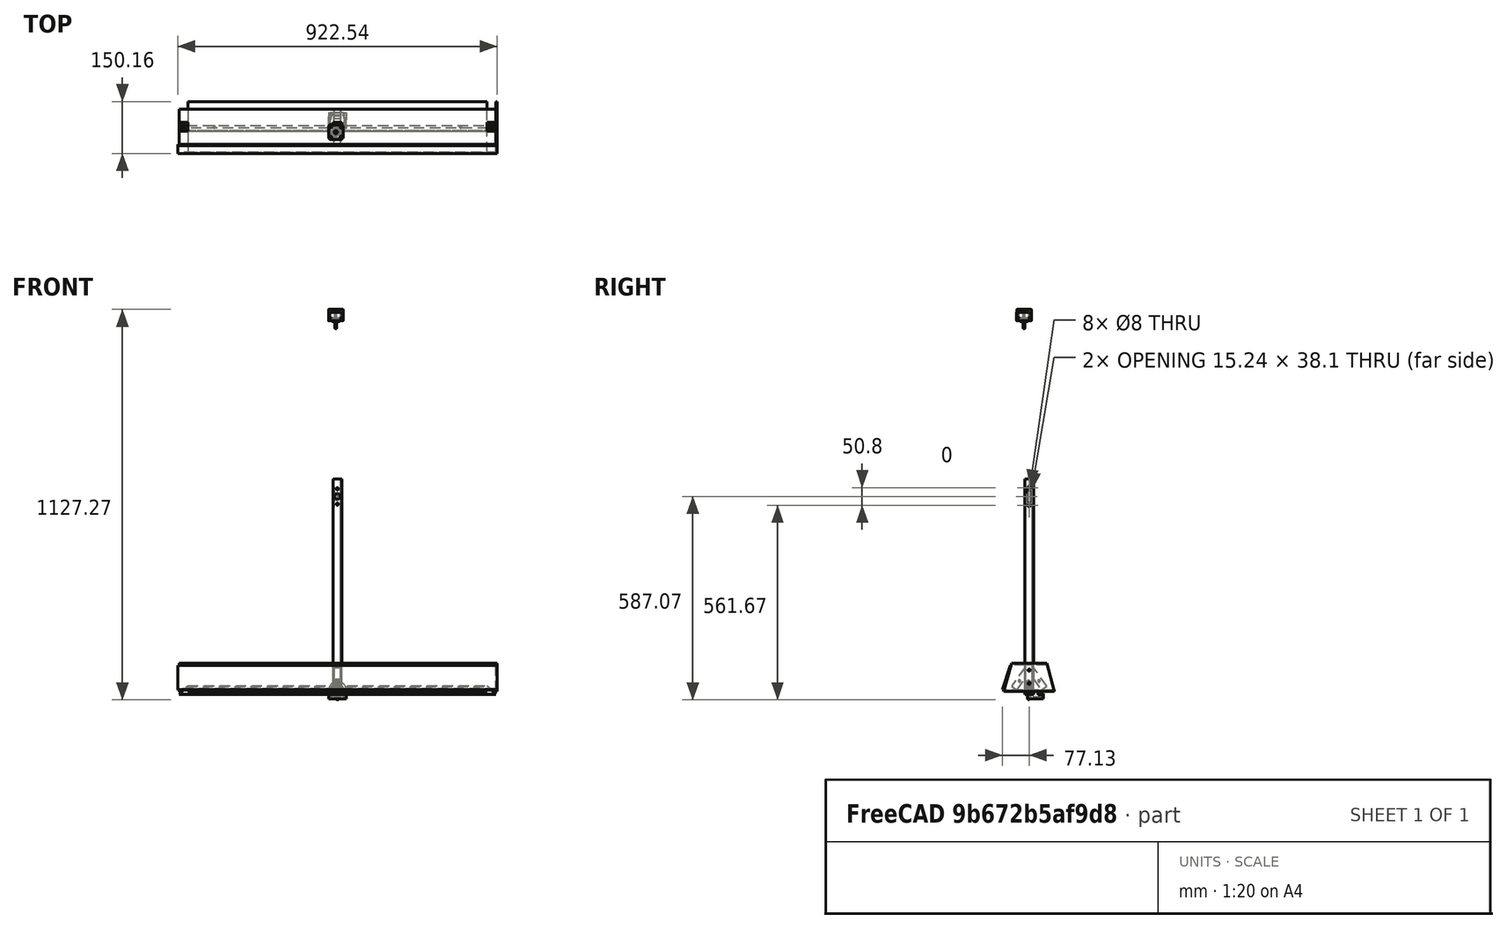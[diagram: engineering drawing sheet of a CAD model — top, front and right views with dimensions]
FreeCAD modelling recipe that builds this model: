
FCSTD DOCUMENT  (FreeCAD 0.21R32637 (Git))
Label: Frame
License: All rights reserved
LicenseURL: http://en.wikipedia.org/wiki/All_rights_reserved
objects: Sketcher::SketchObject×37, PartDesign::Pocket×19, PartDesign::Pad×17, PartDesign::CoordinateSystem×17, TechDraw::DrawViewDimension×16, PartDesign::Body×15, App::Link×8, App::DocumentObjectGroup×3, PartDesign::Plane×3, TechDraw::DrawViewPart×3, TechDraw::DrawSVGTemplate×2, TechDraw::DrawProjGroupItem×2, TechDraw::DrawPage×2, PartDesign::Fillet×2, App::FeaturePython×1, Part::Feature×1, PartDesign::FeatureBase×1, App::Part×1, TechDraw::DrawProjGroup×1, TechDraw::DrawViewDetail×1, +3 more types
note: 173 computed .brp shape members not serialized (recipe doc carries the construction recipe); baked Part::Feature solids carry a one-line shape summary decoded from their .brp

FEATURE [Sketcher::SketchObject] Sketch
  FullyConstrained = true
  MapMode = 5
  Support = -> [XY_Plane]
  sketch-geometry (15):
    g0: LineSegment StartX=-12.7 StartY=-12.7 StartZ=0 EndX=-12.7 EndY=12.7 EndZ=0
    g1: LineSegment StartX=-12.7 StartY=12.7 StartZ=0 EndX=12.7 EndY=12.7 EndZ=0
    g2: LineSegment StartX=12.7 StartY=12.7 StartZ=0 EndX=12.7 EndY=-12.7 EndZ=0
    g3: LineSegment StartX=12.7 StartY=-12.7 StartZ=0 EndX=-12.7 EndY=-12.7 EndZ=0
    g4: GeomPoint X=0 Y=0 Z=0
    g5: ArcOfCircle CenterX=-6.35 CenterY=-6.35 CenterZ=0 NormalX=0 NormalY=0 NormalZ=1 AngleXU=0 Radius=3.175 StartAngle=3.14159 EndAngle=4.71239
    g6: LineSegment StartX=-9.525 StartY=-6.35 StartZ=0 EndX=-9.525 EndY=6.35 EndZ=0
    g7: ArcOfCircle CenterX=-6.35 CenterY=6.35 CenterZ=0 NormalX=0 NormalY=0 NormalZ=1 AngleXU=0 Radius=3.175 StartAngle=1.5708 EndAngle=3.14159
    g8: LineSegment StartX=-6.35 StartY=9.525 StartZ=0 EndX=6.35 EndY=9.525 EndZ=0
    g9: ArcOfCircle CenterX=6.35 CenterY=6.35 CenterZ=0 NormalX=0 NormalY=0 NormalZ=1 AngleXU=0 Radius=3.175 StartAngle=3e-16 EndAngle=1.5708
    g10: LineSegment StartX=9.525 StartY=6.35 StartZ=0 EndX=9.525 EndY=-6.35 EndZ=0
    g11: ArcOfCircle CenterX=6.35 CenterY=-6.35 CenterZ=0 NormalX=0 NormalY=0 NormalZ=1 AngleXU=0 Radius=3.175 StartAngle=4.71239 EndAngle=6.28319
    g12: LineSegment StartX=6.35 StartY=-9.525 StartZ=0 EndX=-6.35 EndY=-9.525 EndZ=0
    g13: GeomPoint X=-9.525 Y=-9.525 Z=0
    g14: GeomPoint X=9.525 Y=9.525 Z=0
  constraints (35):
    c: Coincident(g0,g1)
    c: Coincident(g1,g2)
    c: Coincident(g2,g3)
    c: Coincident(g3,g0)
    c: Horizontal(g1)
    c: Horizontal(g3)
    c: Vertical(g0)
    c: Vertical(g2)
    c: Symmetric(g1,g0,g4)
    c: Coincident(g4,g-1)
    c: Equal(g1,g2)
    c: Distance(g1) = 25.4
    c: Tangent(g5,g6) = 1.5708
    c: Tangent(g6,g7) = 1.5708
    c: Tangent(g7,g8) = 1.5708
    c: Tangent(g8,g9) = 1.5708
    c: Tangent(g9,g10) = 1.5708
    c: Tangent(g10,g11) = 1.5708
    c: Tangent(g11,g12) = 1.5708
    c: Tangent(g12,g5) = 1.5708
    c: Horizontal(g8)
    c: Horizontal(g12)
    c: Vertical(g6)
    c: Vertical(g10)
    c: Equal(g5,g7)
    c: Equal(g7,g9)
    c: Equal(g9,g11)
    c: PointOnObject(g13,g6)
    c: PointOnObject(g13,g12)
    c: PointOnObject(g14,g8)
    c: PointOnObject(g14,g10)
    c: Radius(g9) = 3.175
    c: Symmetric(g7,g11,g4)
    c: Distance(g7,g1) = 3.175
    c: Equal(g8,g6)
FEATURE [PartDesign::Pad] Pad
  Direction = (0,0,1)
  Length = 609.6
  Length2 = 10
  Profile = -> Sketch
  ReferenceAxis = -> Sketch [N_Axis]
  Type = 0
FEATURE [PartDesign::Body] Body  label="Base Extrusion"
  Group = -> [Sketch,Pad]
  Origin = -> Origin
  Tip = -> Pad
FEATURE [Sketcher::SketchObject] Sketch001
  FullyConstrained = true
  MapMode = 5
  Support = -> [XY_Plane001]
  sketch-geometry (15):
    g0: LineSegment StartX=-12.7 StartY=-12.7 StartZ=0 EndX=-12.7 EndY=12.7 EndZ=0
    g1: LineSegment StartX=-12.7 StartY=12.7 StartZ=0 EndX=12.7 EndY=12.7 EndZ=0
    g2: LineSegment StartX=12.7 StartY=12.7 StartZ=0 EndX=12.7 EndY=-12.7 EndZ=0
    g3: LineSegment StartX=12.7 StartY=-12.7 StartZ=0 EndX=-12.7 EndY=-12.7 EndZ=0
    g4: GeomPoint X=0 Y=0 Z=0
    g5: ArcOfCircle CenterX=-6.35 CenterY=-6.35 CenterZ=0 NormalX=0 NormalY=0 NormalZ=1 AngleXU=0 Radius=3.175 StartAngle=3.14159 EndAngle=4.71239
    g6: LineSegment StartX=-9.525 StartY=-6.35 StartZ=0 EndX=-9.525 EndY=6.35 EndZ=0
    g7: ArcOfCircle CenterX=-6.35 CenterY=6.35 CenterZ=0 NormalX=0 NormalY=0 NormalZ=1 AngleXU=0 Radius=3.175 StartAngle=1.5708 EndAngle=3.14159
    g8: LineSegment StartX=-6.35 StartY=9.525 StartZ=0 EndX=6.35 EndY=9.525 EndZ=0
    g9: ArcOfCircle CenterX=6.35 CenterY=6.35 CenterZ=0 NormalX=0 NormalY=0 NormalZ=1 AngleXU=0 Radius=3.175 StartAngle=3e-16 EndAngle=1.5708
    g10: LineSegment StartX=9.525 StartY=6.35 StartZ=0 EndX=9.525 EndY=-6.35 EndZ=0
    g11: ArcOfCircle CenterX=6.35 CenterY=-6.35 CenterZ=0 NormalX=0 NormalY=0 NormalZ=1 AngleXU=0 Radius=3.175 StartAngle=4.71239 EndAngle=6.28319
    g12: LineSegment StartX=6.35 StartY=-9.525 StartZ=0 EndX=-6.35 EndY=-9.525 EndZ=0
    g13: GeomPoint X=-9.525 Y=-9.525 Z=0
    g14: GeomPoint X=9.525 Y=9.525 Z=0
  constraints (35):
    c: Coincident(g0,g1)
    c: Coincident(g1,g2)
    c: Coincident(g2,g3)
    c: Coincident(g3,g0)
    c: Horizontal(g1)
    c: Horizontal(g3)
    c: Vertical(g0)
    c: Vertical(g2)
    c: Symmetric(g1,g0,g4)
    c: Coincident(g4,g-1)
    c: Equal(g1,g2)
    c: Distance(g1) = 25.4
    c: Tangent(g5,g6) = 1.5708
    c: Tangent(g6,g7) = 1.5708
    c: Tangent(g7,g8) = 1.5708
    c: Tangent(g8,g9) = 1.5708
    c: Tangent(g9,g10) = 1.5708
    c: Tangent(g10,g11) = 1.5708
    c: Tangent(g11,g12) = 1.5708
    c: Tangent(g12,g5) = 1.5708
    c: Horizontal(g8)
    c: Horizontal(g12)
    c: Vertical(g6)
    c: Vertical(g10)
    c: Equal(g5,g7)
    c: Equal(g7,g9)
    c: Equal(g9,g11)
    c: PointOnObject(g13,g6)
    c: PointOnObject(g13,g12)
    c: PointOnObject(g14,g8)
    c: PointOnObject(g14,g10)
    c: Radius(g9) = 3.175
    c: Symmetric(g7,g11,g4)
    c: Distance(g7,g1) = 3.175
    c: Equal(g8,g6)
FEATURE [PartDesign::Pad] Pad001
  Direction = (0,0,1)
  Length = 609.6
  Length2 = 10
  Profile = -> Sketch001
  ReferenceAxis = -> Sketch001 [N_Axis]
  Type = 0
FEATURE [Sketcher::SketchObject] Sketch002
  ExternalGeometry = -> [Pad001]
  FullyConstrained = true
  MapMode = 5
  Placement = pos=(0,12.7,0) rot=(0,0.707107,0.707107;3.14159rad)
  Support = -> [Pad001]
  sketch-geometry (8):
    g0: LineSegment StartX=0 StartY=580.72 StartZ=0 EndX=-21.9203 EndY=558.8 EndZ=0
    g1: LineSegment StartX=-21.9203 StartY=558.8 StartZ=0 EndX=0 EndY=536.88 EndZ=0
    g2: LineSegment StartX=0 StartY=536.88 StartZ=0 EndX=21.9203 EndY=558.8 EndZ=0
    g3: LineSegment StartX=21.9203 StartY=558.8 StartZ=0 EndX=0 EndY=580.72 EndZ=0
    g4: LineSegment StartX=21.9203 StartY=558.8 StartZ=0 EndX=-21.9203 EndY=558.8 EndZ=0
    g5: Circle CenterX=0 CenterY=558.8 CenterZ=0 NormalX=0 NormalY=0 NormalZ=1 AngleXU=0 Radius=8.89
    g6: Circle CenterX=0 CenterY=580.72 CenterZ=0 NormalX=0 NormalY=0 NormalZ=1 AngleXU=0 Radius=1.6
    g7: Circle CenterX=0 CenterY=536.88 CenterZ=0 NormalX=0 NormalY=0 NormalZ=1 AngleXU=0 Radius=1.6
  constraints (21):
    c: PointOnObject(g0,g-2)
    c: Coincident(g1,g0)
    c: PointOnObject(g1,g-2)
    c: Coincident(g2,g1)
    c: Coincident(g3,g2)
    c: Coincident(g3,g0)
    c: Perpendicular(g3,g0)
    c: Perpendicular(g2,g1)
    c: Perpendicular(g1,g0)
    c: Coincident(g4,g2)
    c: Coincident(g4,g0)
    c: Horizontal(g4)
    c: Distance(g3) = 31
    c: PointOnObject(g5,g4)
    c: Coincident(g6,g0)
    c: Coincident(g7,g1)
    c: PointOnObject(g5,g-2)
    c: Equal(g7,g6)
    c: Diameter(g6) = 3.2
    c: Diameter(g5) = 17.78
    c: Distance(g5,g-3) = 50.8
FEATURE [PartDesign::Pocket] Pocket
  BaseFeature = -> Pad001
  Direction = (0,-1,2e-16)
  Length = 5.08
  Length2 = 5
  Profile = -> Sketch002
  ReferenceAxis = -> Sketch002 [N_Axis]
  Type = 0
FEATURE [Sketcher::SketchObject] Sketch003
  ExternalGeometry = -> [Pocket]
  FullyConstrained = true
  MapMode = 5
  Placement = pos=(-12.7,0,0) rot=(0.57735,-0.57735,-0.57735;2.0944rad)
  Support = -> [Pocket]
  sketch-geometry (2):
    g0: Circle CenterX=0 CenterY=584.2 CenterZ=0 NormalX=0 NormalY=0 NormalZ=1 AngleXU=0 Radius=4
    g1: Circle CenterX=0 CenterY=533.4 CenterZ=0 NormalX=0 NormalY=0 NormalZ=1 AngleXU=0 Radius=4
  constraints (6):
    c: PointOnObject(g0,g-2)
    c: PointOnObject(g1,g-2)
    c: Equal(g1,g0)
    c: Diameter(g0) = 8
    c: Distance(g0,g1) = 50.8
    c: Distance(g0,g-3) = 25.4
FEATURE [PartDesign::Pocket] Pocket001
  BaseFeature = -> Pocket
  Direction = (1,0,0)
  Length = 5
  Length2 = 5
  Profile = -> Sketch003
  ReferenceAxis = -> Sketch003 [N_Axis]
  Type = 1
FEATURE [Sketcher::SketchObject] Sketch004
  ExternalGeometry = -> [Pocket001]
  FullyConstrained = true
  MapMode = 5
  Placement = pos=(0,-12.7,0) rot=(1,0,0;1.5708rad)
  Support = -> [Pocket001]
  sketch-geometry (3):
    g0: LineSegment StartX=12.7 StartY=0 StartZ=0 EndX=-12.7 EndY=0 EndZ=0
    g1: LineSegment StartX=-12.7 StartY=0 StartZ=0 EndX=-12.7 EndY=25.4 EndZ=0
    g2: LineSegment StartX=-12.7 StartY=25.4 StartZ=0 EndX=12.7 EndY=0 EndZ=0
  constraints (7):
    c: Coincident(g0,g-3)
    c: Coincident(g1,g0)
    c: Vertical(g1)
    c: Coincident(g2,g1)
    c: Coincident(g2,g0)
    c: Equal(g1,g0)
    c: Coincident(g-4,g0)
FEATURE [PartDesign::Pocket] Pocket002
  BaseFeature = -> Pocket001
  Direction = (0,1,-2e-16)
  Length = 5
  Length2 = 5
  Profile = -> Sketch004
  ReferenceAxis = -> Sketch004 [N_Axis]
  Type = 1
FEATURE [PartDesign::CoordinateSystem] Local_CS  label="MotorWeldLCS"
  AttacherType = Attacher::AttachEngine3D
  MapMode = 45
  Placement = pos=(2.4e-14,-3.168e-13,12.7) rot=(0.357407,0.357407,0.862856;1.71777rad)
  Support = -> [Pocket002]
FEATURE [PartDesign::CoordinateSystem] Local_CS001  label="MotorLCS"
  AttacherType = Attacher::AttachEngine3D
  MapMode = 11
  Placement = pos=(0,12.7,558.8) rot=(0.57735,0.57735,0.57735;4.18879rad)
  Support = -> [Pocket002]
FEATURE [PartDesign::CoordinateSystem] Local_CS002  label="LowerRailLCS"
  AttacherType = Attacher::AttachEngine3D
  MapMode = 11
  Placement = pos=(12.7,0,533.4) rot=(0,-1,0;1.5708rad)
  Support = -> [Pocket002]
FEATURE [PartDesign::CoordinateSystem] Local_CS003  label="UpperRailLCS"
  AttacherType = Attacher::AttachEngine3D
  MapMode = 11
  Placement = pos=(12.7,0,584.2) rot=(0,-1,0;1.5708rad)
  Support = -> [Pocket002]
FEATURE [Sketcher::SketchObject] Sketch005
  FullyConstrained = true
  MapMode = 5
  Support = -> [XY_Plane002]
  sketch-geometry (15):
    g0: LineSegment StartX=-12.7 StartY=-12.7 StartZ=0 EndX=-12.7 EndY=12.7 EndZ=0
    g1: LineSegment StartX=-12.7 StartY=12.7 StartZ=0 EndX=12.7 EndY=12.7 EndZ=0
    g2: LineSegment StartX=12.7 StartY=12.7 StartZ=0 EndX=12.7 EndY=-12.7 EndZ=0
    g3: LineSegment StartX=12.7 StartY=-12.7 StartZ=0 EndX=-12.7 EndY=-12.7 EndZ=0
    g4: GeomPoint X=0 Y=0 Z=0
    g5: ArcOfCircle CenterX=-6.35 CenterY=-6.35 CenterZ=0 NormalX=0 NormalY=0 NormalZ=1 AngleXU=0 Radius=3.175 StartAngle=3.14159 EndAngle=4.71239
    g6: LineSegment StartX=-9.525 StartY=-6.35 StartZ=0 EndX=-9.525 EndY=6.35 EndZ=0
    g7: ArcOfCircle CenterX=-6.35 CenterY=6.35 CenterZ=0 NormalX=0 NormalY=0 NormalZ=1 AngleXU=0 Radius=3.175 StartAngle=1.5708 EndAngle=3.14159
    g8: LineSegment StartX=-6.35 StartY=9.525 StartZ=0 EndX=6.35 EndY=9.525 EndZ=0
    g9: ArcOfCircle CenterX=6.35 CenterY=6.35 CenterZ=0 NormalX=0 NormalY=0 NormalZ=1 AngleXU=0 Radius=3.175 StartAngle=3e-16 EndAngle=1.5708
    g10: LineSegment StartX=9.525 StartY=6.35 StartZ=0 EndX=9.525 EndY=-6.35 EndZ=0
    g11: ArcOfCircle CenterX=6.35 CenterY=-6.35 CenterZ=0 NormalX=0 NormalY=0 NormalZ=1 AngleXU=0 Radius=3.175 StartAngle=4.71239 EndAngle=6.28319
    g12: LineSegment StartX=6.35 StartY=-9.525 StartZ=0 EndX=-6.35 EndY=-9.525 EndZ=0
    g13: GeomPoint X=-9.525 Y=-9.525 Z=0
    g14: GeomPoint X=9.525 Y=9.525 Z=0
  constraints (35):
    c: Coincident(g0,g1)
    c: Coincident(g1,g2)
    c: Coincident(g2,g3)
    c: Coincident(g3,g0)
    c: Horizontal(g1)
    c: Horizontal(g3)
    c: Vertical(g0)
    c: Vertical(g2)
    c: Symmetric(g1,g0,g4)
    c: Coincident(g4,g-1)
    c: Equal(g1,g2)
    c: Distance(g1) = 25.4
    c: Tangent(g5,g6) = 1.5708
    c: Tangent(g6,g7) = 1.5708
    c: Tangent(g7,g8) = 1.5708
    c: Tangent(g8,g9) = 1.5708
    c: Tangent(g9,g10) = 1.5708
    c: Tangent(g10,g11) = 1.5708
    c: Tangent(g11,g12) = 1.5708
    c: Tangent(g12,g5) = 1.5708
    c: Horizontal(g8)
    c: Horizontal(g12)
    c: Vertical(g6)
    c: Vertical(g10)
    c: Equal(g5,g7)
    c: Equal(g7,g9)
    c: Equal(g9,g11)
    c: PointOnObject(g13,g6)
    c: PointOnObject(g13,g12)
    c: PointOnObject(g14,g8)
    c: PointOnObject(g14,g10)
    c: Radius(g9) = 3.175
    c: Symmetric(g7,g11,g4)
    c: Distance(g7,g1) = 3.175
    c: Equal(g8,g6)
FEATURE [PartDesign::Pad] Pad002
  Direction = (0,0,1)
  Length = 609.6
  Length2 = 10
  Profile = -> Sketch005
  ReferenceAxis = -> Sketch005 [N_Axis]
  Type = 0
FEATURE [Sketcher::SketchObject] Sketch006
  ExternalGeometry = -> [Pad002]
  FullyConstrained = true
  MapMode = 5
  Placement = pos=(12.7,0,0) rot=(0.57735,0.57735,0.57735;2.0944rad)
  Support = -> [Pad002]
  sketch-geometry (2):
    g0: Circle CenterX=0 CenterY=584.2 CenterZ=0 NormalX=0 NormalY=0 NormalZ=1 AngleXU=0 Radius=4
    g1: Circle CenterX=0 CenterY=533.4 CenterZ=0 NormalX=0 NormalY=0 NormalZ=1 AngleXU=0 Radius=4
  constraints (6):
    c: PointOnObject(g0,g-2)
    c: PointOnObject(g1,g-2)
    c: Equal(g1,g0)
    c: Diameter(g0) = 8
    c: Distance(g0,g-3) = 25.4
    c: Distance(g0,g1) = 50.8
FEATURE [PartDesign::Pocket] Pocket003
  BaseFeature = -> Pad002
  Direction = (-1,0,0)
  Length = 5
  Length2 = 5
  Profile = -> Sketch006
  ReferenceAxis = -> Sketch006 [N_Axis]
  Type = 1
FEATURE [Sketcher::SketchObject] Sketch007
  ExternalGeometry = -> [Pocket003]
  FullyConstrained = true
  MapMode = 5
  Placement = pos=(0,-12.7,0) rot=(1,0,0;1.5708rad)
  Support = -> [Pocket003]
  sketch-geometry (3):
    g0: LineSegment StartX=12.7 StartY=25.4 StartZ=0 EndX=-12.7 EndY=0 EndZ=0
    g1: LineSegment StartX=12.7 StartY=25.4 StartZ=0 EndX=12.7 EndY=0 EndZ=0
    g2: LineSegment StartX=12.7 StartY=0 StartZ=0 EndX=-12.7 EndY=0 EndZ=0
  constraints (7):
    c: PointOnObject(g0,g-4)
    c: Coincident(g1,g0)
    c: Coincident(g1,g-4)
    c: Coincident(g2,g1)
    c: Coincident(g2,g0)
    c: Equal(g1,g2)
    c: Coincident(g0,g-3)
FEATURE [PartDesign::Pocket] Pocket004
  BaseFeature = -> Pocket003
  Direction = (0,1,-2e-16)
  Length = 5
  Length2 = 5
  Profile = -> Sketch007
  ReferenceAxis = -> Sketch007 [N_Axis]
  Type = 1
FEATURE [PartDesign::CoordinateSystem] Local_CS004  label="EndWeldLCS"
  AttacherType = Attacher::AttachEngine3D
  MapMode = 45
  Placement = pos=(2.49e-14,3.02e-14,12.7) rot=(-0.357407,-0.357407,0.862856;1.71777rad)
  Support = -> [Pocket004]
FEATURE [Sketcher::SketchObject] Sketch008
  FullyConstrained = true
  MapMode = 5
  Placement = pos=(0,0,0) rot=(0.57735,0.57735,0.57735;2.0944rad)
  Support = -> [YZ_Plane003]
  sketch-geometry (15):
    g0: LineSegment StartX=-12.7 StartY=-12.7 StartZ=0 EndX=-12.7 EndY=12.7 EndZ=0
    g1: LineSegment StartX=-12.7 StartY=12.7 StartZ=0 EndX=12.7 EndY=12.7 EndZ=0
    g2: LineSegment StartX=12.7 StartY=12.7 StartZ=0 EndX=12.7 EndY=-12.7 EndZ=0
    g3: LineSegment StartX=12.7 StartY=-12.7 StartZ=0 EndX=-12.7 EndY=-12.7 EndZ=0
    g4: GeomPoint X=0 Y=0 Z=0
    g5: ArcOfCircle CenterX=-6.35 CenterY=-6.35 CenterZ=0 NormalX=0 NormalY=0 NormalZ=1 AngleXU=0 Radius=3.175 StartAngle=3.14159 EndAngle=4.71239
    g6: LineSegment StartX=-9.525 StartY=-6.35 StartZ=0 EndX=-9.525 EndY=6.35 EndZ=0
    g7: ArcOfCircle CenterX=-6.35 CenterY=6.35 CenterZ=0 NormalX=0 NormalY=0 NormalZ=1 AngleXU=0 Radius=3.175 StartAngle=1.5708 EndAngle=3.14159
    g8: LineSegment StartX=-6.35 StartY=9.525 StartZ=0 EndX=6.35 EndY=9.525 EndZ=0
    g9: ArcOfCircle CenterX=6.35 CenterY=6.35 CenterZ=0 NormalX=0 NormalY=0 NormalZ=1 AngleXU=0 Radius=3.175 StartAngle=2e-16 EndAngle=1.5708
    g10: LineSegment StartX=9.525 StartY=6.35 StartZ=0 EndX=9.525 EndY=-6.35 EndZ=0
    g11: ArcOfCircle CenterX=6.35 CenterY=-6.35 CenterZ=0 NormalX=0 NormalY=0 NormalZ=1 AngleXU=0 Radius=3.175 StartAngle=4.71239 EndAngle=6.28319
    g12: LineSegment StartX=6.35 StartY=-9.525 StartZ=0 EndX=-6.35 EndY=-9.525 EndZ=0
    g13: GeomPoint X=-9.525 Y=-9.525 Z=0
    g14: GeomPoint X=9.525 Y=9.525 Z=0
  constraints (35):
    c: Coincident(g0,g1)
    c: Coincident(g1,g2)
    c: Coincident(g2,g3)
    c: Coincident(g3,g0)
    c: Horizontal(g1)
    c: Horizontal(g3)
    c: Vertical(g0)
    c: Vertical(g2)
    c: Symmetric(g1,g0,g4)
    c: Coincident(g4,g-1)
    c: Tangent(g5,g6) = 1.5708
    c: Tangent(g6,g7) = 1.5708
    c: Tangent(g7,g8) = 1.5708
    c: Tangent(g8,g9) = 1.5708
    c: Tangent(g9,g10) = 1.5708
    c: Tangent(g10,g11) = 1.5708
    c: Tangent(g11,g12) = 1.5708
    c: Tangent(g12,g5) = 1.5708
    c: Horizontal(g8)
    c: Horizontal(g12)
    c: Vertical(g6)
    c: Vertical(g10)
    c: Equal(g5,g7)
    c: Equal(g7,g9)
    c: Equal(g9,g11)
    c: PointOnObject(g13,g6)
    c: PointOnObject(g13,g12)
    c: PointOnObject(g14,g8)
    c: PointOnObject(g14,g10)
    c: Equal(g8,g6)
    c: Equal(g1,g0)
    c: Symmetric(g9,g5,g4)
    c: Radius(g11) = 3.175
    c: Distance(g10,g2) = 3.175
    c: Distance(g2) = 25.4
FEATURE [PartDesign::Pad] Pad003  label="OverallLength"
  Direction = (1,-2e-16,3e-16)
  Length = 914.4
  Length2 = 10
  Midplane = true
  Placement = pos=(0,0,0) rot=(0.57735,0.57735,0.57735;2.0944rad)
  Profile = -> Sketch008
  ReferenceAxis = -> Sketch008 [N_Axis]
  Type = 0
FEATURE [Sketcher::SketchObject] Sketch009
  ExternalGeometry = -> [Pad003]
  FullyConstrained = true
  MapMode = 5
  Placement = pos=(-5.6e-15,-12.7,2.8e-15) rot=(-0.57735,-0.57735,0.57735;4.18879rad)
  Support = -> [Pad003]
  sketch-geometry (6):
    g0: LineSegment StartX=12.7 StartY=457.2 StartZ=0 EndX=-12.7 EndY=457.2 EndZ=0
    g1: LineSegment StartX=-12.7 StartY=457.2 StartZ=0 EndX=-12.7 EndY=431.8 EndZ=0
    g2: LineSegment StartX=-12.7 StartY=431.8 StartZ=0 EndX=12.7 EndY=457.2 EndZ=0
    g3: LineSegment StartX=12.7 StartY=-457.2 StartZ=0 EndX=-12.7 EndY=-457.2 EndZ=0
    g4: LineSegment StartX=-12.7 StartY=-457.2 StartZ=0 EndX=-12.7 EndY=-431.8 EndZ=0
    g5: LineSegment StartX=-12.7 StartY=-431.8 StartZ=0 EndX=12.7 EndY=-457.2 EndZ=0
  constraints (14):
    c: Coincident(g0,g-5)
    c: Coincident(g0,g-4)
    c: Coincident(g1,g0)
    c: PointOnObject(g1,g-4)
    c: Coincident(g2,g1)
    c: Coincident(g2,g0)
    c: Coincident(g3,g-3)
    c: Coincident(g3,g-4)
    c: Coincident(g4,g3)
    c: PointOnObject(g4,g-4)
    c: Coincident(g5,g4)
    c: Coincident(g5,g3)
    c: Equal(g1,g0)
    c: Equal(g0,g4)
FEATURE [PartDesign::Pocket] Pocket005
  BaseFeature = -> Pad003
  Direction = (4e-16,1,-2e-16)
  Length = 5
  Length2 = 5
  Placement = pos=(0,0,0) rot=(0.57735,0.57735,0.57735;2.0944rad)
  Profile = -> Sketch009
  ReferenceAxis = -> Sketch009 [N_Axis]
  Type = 1
FEATURE [PartDesign::CoordinateSystem] Local_CS005  label="LeftLCS"
  AttacherType = Attacher::AttachEngine3D
  MapMode = 45
  Placement = pos=(-444.5,3.845e-13,-8.53e-14) rot=(-0.357407,-0.357407,0.862856;1.71777rad)
  Support = -> [Pocket005]
FEATURE [PartDesign::CoordinateSystem] Local_CS006  label="RightLCS"
  AttacherType = Attacher::AttachEngine3D
  MapMode = 45
  Placement = pos=(444.5,-6.185e-13,0) rot=(0.357407,0.357407,0.862856;1.71777rad)
  Support = -> [Pocket005]
FEATURE [PartDesign::CoordinateSystem] Local_CS007
  AttacherType = Attacher::AttachEngine3D
  MapMode = 5
  Placement = pos=(3.6e-15,-5.6e-15,-12.7) rot=(0.707107,0.707107,0;3.14159rad)
  Support = -> [Pocket005]
FEATURE [PartDesign::Body] Body003  label="Lower Extrusion"
  Group = -> [Sketch008,Pad003,Sketch009,Pocket005,Local_CS005,Local_CS006,Local_CS007]
  Origin = -> Origin003
  Tip = -> Pocket005
FEATURE [PartDesign::CoordinateSystem] LCS_Origin
  AttacherType = Attacher::AttachEngine3D
  MapMode = 2
  Support = -> [X_Axis004]
FEATURE [App::DocumentObjectGroup] Constraints
FEATURE [App::FeaturePython] Variables  # WARN: FeaturePython — macro-defined, semantics opaque (R4)
  Type = App::PropertyContainer
FEATURE [App::DocumentObjectGroup] Configurations
FEATURE [App::Link] Lower_Extrusion  label="Lower Extrusion001"
  AssemblyType = Part::Link
  AttachedBy = #Local_CS007
  AttachedTo = Parent Assembly#LCS_Origin
  AttachmentOffset = pos=(0,0,0) rot=(-0.707107,-0.707107,0;3.14159rad)
  LinkPlacement = pos=(1.2e-15,-1.2e-15,12.7) rot=(0,0,1;0rad)
  LinkedObject = -> Body003
  Placement = pos=(1.2e-15,-1.2e-15,12.7) rot=(0,0,1;0rad)
  SolverId = Asm4EE
  expr: Placement = LCS_Origin.Placement * AttachmentOffset * Local_CS007.Placement ^ -1
FEATURE [App::Link] Motor_Extrusion  label="Motor Extrusion001"
  AssemblyType = Part::Link
  AttachedBy = #Local_CS
  AttachedTo = Lower_Extrusion#Local_CS006
  LinkPlacement = pos=(444.5,-4.264e-13,-6.75e-14) rot=(0,0,1;0rad)
  LinkedObject = -> Body001
  Placement = pos=(444.5,-4.264e-13,-6.75e-14) rot=(0,0,1;0rad)
  SolverId = Asm4EE
  expr: Placement = Lower_Extrusion.Placement * Local_CS006.Placement * AttachmentOffset * Local_CS.Placement ^ -1
FEATURE [App::Link] Endplate_Extrusion  label="Endplate Extrusion001"
  AssemblyType = Part::Link
  AttachedBy = #Local_CS004
  AttachedTo = Lower_Extrusion#Local_CS005
  LinkPlacement = pos=(-444.5,4.549e-13,-2.043e-13) rot=(0,0,1;0rad)
  LinkedObject = -> Body002
  Placement = pos=(-444.5,4.549e-13,-2.043e-13) rot=(0,0,1;0rad)
  SolverId = Asm4EE
  expr: Placement = Lower_Extrusion.Placement * Local_CS005.Placement * AttachmentOffset * Local_CS004.Placement ^ -1
FEATURE [Sketcher::SketchObject] Sketch010
  ExternalGeometry = -> [Pocket002]
  FullyConstrained = true
  MapMode = 5
  Placement = pos=(12.7,0,0) rot=(0.57735,0.57735,0.57735;2.0944rad)
  Support = -> [Pocket002]
  sketch-geometry (12):
    g0: ArcOfCircle CenterX=-2.8575 CenterY=544.513 CenterZ=0 NormalX=0 NormalY=0 NormalZ=1 AngleXU=0 Radius=4.7625 StartAngle=3.14159 EndAngle=4.71239
    g1: LineSegment StartX=-7.62 StartY=544.513 StartZ=0 EndX=-7.62 EndY=573.088 EndZ=0
    g2: ArcOfCircle CenterX=-2.8575 CenterY=573.088 CenterZ=0 NormalX=0 NormalY=0 NormalZ=1 AngleXU=0 Radius=4.7625 StartAngle=1.5708 EndAngle=3.14159
    g3: LineSegment StartX=-2.8575 StartY=577.85 StartZ=0 EndX=2.8575 EndY=577.85 EndZ=0
    g4: ArcOfCircle CenterX=2.8575 CenterY=573.088 CenterZ=0 NormalX=0 NormalY=0 NormalZ=1 AngleXU=0 Radius=4.7625 StartAngle=-5.3e-15 EndAngle=1.5708
    g5: LineSegment StartX=7.62 StartY=573.088 StartZ=0 EndX=7.62 EndY=544.513 EndZ=0
    g6: ArcOfCircle CenterX=2.8575 CenterY=544.513 CenterZ=0 NormalX=0 NormalY=0 NormalZ=1 AngleXU=0 Radius=4.7625 StartAngle=4.71239 EndAngle=6.28319
    g7: LineSegment StartX=2.8575 StartY=539.75 StartZ=0 EndX=-2.8575 EndY=539.75 EndZ=0
    g8: GeomPoint X=-7.62 Y=539.75 Z=0
    g9: GeomPoint X=7.62 Y=577.85 Z=0
    g10: LineSegment StartX=0 StartY=584.2 StartZ=0 EndX=0 EndY=577.85 EndZ=0
    g11: LineSegment StartX=0 StartY=533.4 StartZ=0 EndX=0 EndY=539.75 EndZ=0
  constraints (29):
    c: Tangent(g0,g1) = 1.5708
    c: Tangent(g1,g2) = 1.5708
    c: Tangent(g2,g3) = 1.5708
    c: Tangent(g3,g4) = 1.5708
    c: Tangent(g4,g5) = 1.5708
    c: Tangent(g5,g6) = 1.5708
    c: Tangent(g6,g7) = 1.5708
    c: Tangent(g7,g0) = 1.5708
    c: Horizontal(g3)
    c: Horizontal(g7)
    c: Vertical(g1)
    c: Vertical(g5)
    c: Equal(g0,g2)
    c: Equal(g4,g6)
    c: PointOnObject(g8,g1)
    c: PointOnObject(g8,g7)
    c: PointOnObject(g9,g3)
    c: PointOnObject(g9,g5)
    c: Radius(g4) = 4.7625
    c: Symmetric(g4,g2,g-2)
    c: Distance(g1,g4) = 15.24
    c: Coincident(g10,g-3)
    c: PointOnObject(g10,g3)
    c: Vertical(g10)
    c: Coincident(g11,g-4)
    c: PointOnObject(g11,g7)
    c: Vertical(g11)
    c: Equal(g11,g10)
    c: Distance(g10) = 6.35
FEATURE [PartDesign::Pocket] Pocket006
  BaseFeature = -> Pocket002
  Direction = (-1,0,0)
  Length = 5
  Length2 = 5
  Profile = -> Sketch010
  ReferenceAxis = -> Sketch010 [N_Axis]
  Type = 1
FEATURE [App::Link] NEMA17  label="NEMA018"
  AssemblyType = Part::Link
  AttachedBy = #Local_CS008
  AttachedTo = Motor_Extrusion#Local_CS001
  AttachmentOffset = pos=(0,0,0) rot=(1,0,0;3.14159rad)
  LinkPlacement = pos=(458.43,-1053.3,551.517) rot=(0.862856,0.357407,0.357407;4.56541rad)
  LinkedObject = -> Body004
  Placement = pos=(458.43,-1053.3,551.517) rot=(0.862856,0.357407,0.357407;4.56541rad)
  SolverId = Asm4EE
  expr: Placement = Motor_Extrusion.Placement * Local_CS001.Placement * AttachmentOffset * Local_CS008.Placement ^ -1
FEATURE [Sketcher::SketchObject] Sketch011
  ExternalGeometry = -> [Pocket004]
  FullyConstrained = true
  MapMode = 5
  Placement = pos=(-12.7,0,0) rot=(0.57735,-0.57735,-0.57735;2.0944rad)
  Support = -> [Pocket004]
  sketch-geometry (12):
    g0: ArcOfCircle CenterX=-2.8575 CenterY=544.513 CenterZ=0 NormalX=0 NormalY=0 NormalZ=1 AngleXU=0 Radius=4.7625 StartAngle=3.14159 EndAngle=4.71239
    g1: LineSegment StartX=-7.62 StartY=544.513 StartZ=0 EndX=-7.62 EndY=573.087 EndZ=0
    g2: ArcOfCircle CenterX=-2.8575 CenterY=573.087 CenterZ=0 NormalX=0 NormalY=0 NormalZ=1 AngleXU=0 Radius=4.7625 StartAngle=1.5708 EndAngle=3.14159
    g3: LineSegment StartX=-2.8575 StartY=577.85 StartZ=0 EndX=2.8575 EndY=577.85 EndZ=0
    g4: ArcOfCircle CenterX=2.8575 CenterY=573.087 CenterZ=0 NormalX=0 NormalY=0 NormalZ=1 AngleXU=0 Radius=4.7625 StartAngle=-8.9e-15 EndAngle=1.5708
    g5: LineSegment StartX=7.62 StartY=573.087 StartZ=0 EndX=7.62 EndY=544.513 EndZ=0
    g6: ArcOfCircle CenterX=2.8575 CenterY=544.513 CenterZ=0 NormalX=0 NormalY=0 NormalZ=1 AngleXU=0 Radius=4.7625 StartAngle=4.71239 EndAngle=6.28319
    g7: LineSegment StartX=2.8575 StartY=539.75 StartZ=0 EndX=-2.8575 EndY=539.75 EndZ=0
    g8: GeomPoint X=-7.62 Y=539.75 Z=0
    g9: GeomPoint X=7.62 Y=577.85 Z=0
    g10: LineSegment StartX=0 StartY=577.85 StartZ=0 EndX=0 EndY=584.2 EndZ=0
    g11: LineSegment StartX=0 StartY=539.75 StartZ=0 EndX=0 EndY=533.4 EndZ=0
  constraints (29):
    c: Tangent(g0,g1) = 1.5708
    c: Tangent(g1,g2) = 1.5708
    c: Tangent(g2,g3) = 1.5708
    c: Tangent(g3,g4) = 1.5708
    c: Tangent(g4,g5) = 1.5708
    c: Tangent(g5,g6) = 1.5708
    c: Tangent(g6,g7) = 1.5708
    c: Tangent(g7,g0) = 1.5708
    c: Horizontal(g3)
    c: Vertical(g1)
    c: Vertical(g5)
    c: Equal(g0,g2)
    c: Equal(g2,g4)
    c: Equal(g4,g6)
    c: PointOnObject(g8,g1)
    c: PointOnObject(g8,g7)
    c: PointOnObject(g9,g3)
    c: PointOnObject(g9,g5)
    c: Symmetric(g6,g0,g-2)
    c: Radius(g6) = 4.7625
    c: PointOnObject(g10,g3)
    c: Coincident(g10,g-3)
    c: Vertical(g10)
    c: PointOnObject(g11,g7)
    c: Coincident(g11,g-4)
    c: Vertical(g11)
    c: Equal(g11,g10)
    c: Distance(g10) = 6.35
    c: Distance(g4,g1) = 15.24
FEATURE [PartDesign::Pocket] Pocket007
  BaseFeature = -> Pocket004
  Direction = (1,0,0)
  Length = 5
  Length2 = 5
  Profile = -> Sketch011
  ReferenceAxis = -> Sketch011 [N_Axis]
  Type = 1
FEATURE [Sketcher::SketchObject] Sketch012
  ExternalGeometry = -> [Pocket007]
  FullyConstrained = true
  MapMode = 5
  Placement = pos=(0,-12.7,0) rot=(1,0,0;1.5708rad)
  Support = -> [Pocket007]
  sketch-geometry (2):
    g0: Circle CenterX=0 CenterY=558.8 CenterZ=0 NormalX=0 NormalY=0 NormalZ=1 AngleXU=0 Radius=8.255
    g1: LineSegment StartX=0 StartY=558.8 StartZ=0 EndX=-12.7 EndY=558.8 EndZ=0
  constraints (5):
    c: PointOnObject(g0,g-2)
    c: Diameter(g0) = 16.51
    c: Coincident(g1,g0)
    c: Horizontal(g1)
    c: Symmetric(g-3,g-3,g1)
FEATURE [PartDesign::Pocket] Pocket008
  BaseFeature = -> Pocket007
  Direction = (0,1,-2e-16)
  Length = 5.08
  Length2 = 5
  Profile = -> Sketch012
  ReferenceAxis = -> Sketch012 [N_Axis]
  Type = 0
FEATURE [Sketcher::SketchObject] Sketch013
  ExternalGeometry = -> [Pocket008]
  FullyConstrained = true
  MapMode = 5
  Placement = pos=(0,-12.7,0) rot=(1,0,0;1.5708rad)
  Support = -> [Pocket008]
  sketch-geometry (1):
    g0: Circle CenterX=0 CenterY=558.8 CenterZ=0 NormalX=0 NormalY=0 NormalZ=1 AngleXU=0 Radius=1.5875
  constraints (2):
    c: Coincident(g0,g-3)
    c: Diameter(g0) = 3.175
FEATURE [PartDesign::Pocket] Pocket009
  BaseFeature = -> Pocket008
  Direction = (0,1,-2e-16)
  Length = 5
  Length2 = 5
  Profile = -> Sketch013
  ReferenceAxis = -> Sketch013 [N_Axis]
  Type = 1
FEATURE [PartDesign::Plane] DatumPlane
  AttachmentOffset = pos=(0,0,-3.175) rot=(0,0,1;0rad)
  Length = 60
  MapMode = 5
  Placement = pos=(-9.525,0,0) rot=(0.57735,-0.57735,-0.57735;2.0944rad)
  ResizeMode = 0
  Support = -> [Pocket006]
  Width = 60
FEATURE [Sketcher::SketchObject] Sketch014
  ExternalGeometry = -> [Pocket006]
  FullyConstrained = true
  MapMode = 5
  Placement = pos=(-9.525,0,0) rot=(0.57735,-0.57735,-0.57735;2.0944rad)
  Support = -> [DatumPlane]
  sketch-geometry (9):
    g0: LineSegment StartX=12.7 StartY=31.75 StartZ=0 EndX=12.7 EndY=64.9627 EndZ=0
    g1: LineSegment StartX=12.7 StartY=64.9627 StartZ=0 EndX=50.5364 EndY=10.9266 EndZ=0
    g2: LineSegment StartX=50.5364 StartY=10.9266 StartZ=0 EndX=34.9316 EndY=0 EndZ=0
    g3: LineSegment StartX=34.9316 StartY=0 StartZ=0 EndX=12.7 EndY=31.75 EndZ=0
    g4: LineSegment StartX=-12.7 StartY=64.9627 StartZ=0 EndX=-12.7 EndY=31.75 EndZ=0
    g5: LineSegment StartX=-12.7 StartY=31.75 StartZ=0 EndX=-34.9316 EndY=-7.1e-15 EndZ=0
    g6: LineSegment StartX=-34.9316 StartY=-7.1e-15 StartZ=0 EndX=-50.5364 EndY=10.9266 EndZ=0
    g7: LineSegment StartX=-50.5364 StartY=10.9266 StartZ=0 EndX=-12.7 EndY=64.9627 EndZ=0
    g8: LineSegment StartX=12.7 StartY=31.75 StartZ=0 EndX=-12.7 EndY=31.75 EndZ=0
  constraints (26):
    c: Vertical(g0)
    c: Coincident(g1,g0)
    c: Coincident(g2,g1)
    c: Coincident(g3,g2)
    c: Coincident(g3,g0)
    c: Vertical(g4)
    c: Coincident(g5,g4)
    c: Coincident(g6,g5)
    c: Coincident(g7,g6)
    c: Coincident(g7,g4)
    c: Equal(g4,g0)
    c: Perpendicular(g6,g5)
    c: Perpendicular(g7,g6)
    c: Perpendicular(g2,g3)
    c: Perpendicular(g1,g2)
    c: Coincident(g8,g0)
    c: Horizontal(g8)
    c: Coincident(g4,g8)
    c: PointOnObject(g4,g-4)
    c: PointOnObject(g0,g-3)
    c: Distance(g-3,g0) = 6.35
    c: Distance(g2) = 19.05
    c: Equal(g6,g2)
    c: Equal(g3,g5)
    c: PointOnObject(g2,g-1)
    c: Angle(g3,g-3) = 2.53073
FEATURE [PartDesign::Pad] Pad004
  BaseFeature = -> Pocket006
  Direction = (-1,0,0)
  Length = 19.05
  Length2 = 10
  Profile = -> Sketch014
  ReferenceAxis = -> Sketch014 [N_Axis]
  Reversed = true
  Type = 0
FEATURE [Sketcher::SketchObject] Sketch015
  FullyConstrained = true
  MapMode = 5
  Support = -> [XY_Plane006]
  sketch-geometry (1):
    g0: Circle CenterX=0 CenterY=0 CenterZ=0 NormalX=0 NormalY=0 NormalZ=1 AngleXU=0 Radius=7.62
  constraints (2):
    c: Coincident(g0,g-1)
    c: Diameter(g0) = 15.24
FEATURE [PartDesign::Pad] Pad005
  Direction = (0,0,1)
  Length = 15.24
  Length2 = 10
  Profile = -> Sketch015
  ReferenceAxis = -> Sketch015 [N_Axis]
  Type = 0
FEATURE [PartDesign::Plane] DatumPlane001
  AttachmentOffset = pos=(0,0,-1.27) rot=(0,0,1;0rad)
  Length = 60
  MapMode = 5
  Placement = pos=(0,0,13.97) rot=(0,0,1;0rad)
  ResizeMode = 0
  Support = -> [Pad005]
  Width = 60
FEATURE [Sketcher::SketchObject] Sketch016
  ExternalGeometry = -> [Pad005]
  FullyConstrained = true
  MapMode = 5
  Placement = pos=(0,0,13.97) rot=(0,0,1;0rad)
  Support = -> [DatumPlane001]
  sketch-geometry (18):
    g0: ArcOfCircle CenterX=0 CenterY=7.62 CenterZ=0 NormalX=0 NormalY=0 NormalZ=1 AngleXU=0 Radius=1.27 StartAngle=3.22502 EndAngle=6.19976
    g1: ArcOfCircle CenterX=0 CenterY=0 CenterZ=0 NormalX=0 NormalY=0 NormalZ=1 AngleXU=0 Radius=7.62 StartAngle=1.40394 EndAngle=1.73766
    g2: ArcOfCircle CenterX=7.62 CenterY=0 CenterZ=0 NormalX=0 NormalY=0 NormalZ=1 AngleXU=0 Radius=1.27 StartAngle=1.65423 EndAngle=4.62896
    g3: ArcOfCircle CenterX=0 CenterY=-7.62 CenterZ=0 NormalX=0 NormalY=0 NormalZ=1 AngleXU=0 Radius=1.27 StartAngle=0.0834301 EndAngle=3.05816
    g4: ArcOfCircle CenterX=-7.62 CenterY=0 CenterZ=0 NormalX=0 NormalY=0 NormalZ=1 AngleXU=0 Radius=1.27 StartAngle=4.79582 EndAngle=7.77055
    g5: ArcOfCircle CenterX=-5.38815 CenterY=5.38815 CenterZ=0 NormalX=0 NormalY=0 NormalZ=1 AngleXU=0 Radius=1.27 StartAngle=4.01042 EndAngle=6.98515
    g6: ArcOfCircle CenterX=5.38815 CenterY=5.38815 CenterZ=0 NormalX=0 NormalY=0 NormalZ=1 AngleXU=0 Radius=1.27 StartAngle=2.43962 EndAngle=5.41436
    g7: ArcOfCircle CenterX=5.38815 CenterY=-5.38815 CenterZ=0 NormalX=0 NormalY=0 NormalZ=1 AngleXU=0 Radius=1.27 StartAngle=0.868828 EndAngle=3.84356
    g8: ArcOfCircle CenterX=-5.38815 CenterY=-5.38815 CenterZ=0 NormalX=0 NormalY=0 NormalZ=1 AngleXU=0 Radius=1.27 StartAngle=5.58122 EndAngle=8.55595
    g9: ArcOfCircle CenterX=0 CenterY=0 CenterZ=0 NormalX=0 NormalY=0 NormalZ=1 AngleXU=0 Radius=7.62 StartAngle=2.18933 EndAngle=2.52305
    g10: ArcOfCircle CenterX=0 CenterY=0 CenterZ=0 NormalX=0 NormalY=0 NormalZ=1 AngleXU=0 Radius=7.62 StartAngle=2.97473 EndAngle=3.30845
    g11: ArcOfCircle CenterX=0 CenterY=0 CenterZ=0 NormalX=0 NormalY=0 NormalZ=1 AngleXU=0 Radius=7.62 StartAngle=3.76013 EndAngle=4.09385
    g12: ArcOfCircle CenterX=0 CenterY=0 CenterZ=0 NormalX=0 NormalY=0 NormalZ=1 AngleXU=0 Radius=7.62 StartAngle=6.11633 EndAngle=6.45005
    g13: ArcOfCircle CenterX=0 CenterY=0 CenterZ=0 NormalX=0 NormalY=0 NormalZ=1 AngleXU=0 Radius=7.62 StartAngle=5.33093 EndAngle=5.66465
    g14: ArcOfCircle CenterX=0 CenterY=0 CenterZ=0 NormalX=0 NormalY=0 NormalZ=1 AngleXU=0 Radius=7.62 StartAngle=0.618538 EndAngle=0.952258
    g15: LineSegment StartX=5.38815 StartY=5.38815 StartZ=0 EndX=-5.38815 EndY=-5.38815 EndZ=0
    g16: LineSegment StartX=5.38815 StartY=-5.38815 StartZ=0 EndX=-5.38815 EndY=5.38815 EndZ=0
    g17: ArcOfCircle CenterX=-1.7e-15 CenterY=3.72e-14 CenterZ=0 NormalX=0 NormalY=0 NormalZ=1 AngleXU=0 Radius=7.62 StartAngle=4.54553 EndAngle=4.87925
  constraints (61):
    c: PointOnObject(g0,g-3)
    c: PointOnObject(g0,g-3)
    c: Radius(g0) = 1.27
    c: Coincident(g1,g-3)
    c: Coincident(g1,g0)
    c: Coincident(g1,g0)
    c: PointOnObject(g0,g-2)
    c: PointOnObject(g2,g-3)
    c: PointOnObject(g2,g-3)
    c: PointOnObject(g3,g-3)
    c: PointOnObject(g3,g-3)
    c: PointOnObject(g3,g-3)
    c: PointOnObject(g4,g-3)
    c: PointOnObject(g4,g-3)
    c: PointOnObject(g5,g-3)
    c: PointOnObject(g5,g-3)
    c: PointOnObject(g6,g-3)
    c: PointOnObject(g6,g-3)
    c: PointOnObject(g7,g-3)
    c: PointOnObject(g7,g-3)
    c: PointOnObject(g8,g-3)
    c: PointOnObject(g8,g-3)
    c: Coincident(g9,g1)
    c: Coincident(g9,g5)
    c: Coincident(g9,g5)
    c: Coincident(g10,g1)
    c: Coincident(g10,g4)
    c: Coincident(g10,g4)
    c: Coincident(g11,g1)
    c: Coincident(g11,g8)
    c: Coincident(g11,g8)
    c: Coincident(g12,g1)
    c: Coincident(g12,g2)
    c: Coincident(g12,g2)
    c: Coincident(g13,g1)
    c: Coincident(g13,g7)
    c: Coincident(g13,g7)
    c: Coincident(g14,g1)
    c: Coincident(g14,g6)
    c: Coincident(g14,g6)
    c: Equal(g0,g6)
    c: Equal(g6,g2)
    c: Equal(g2,g7)
    c: Equal(g7,g3)
    c: Equal(g3,g8)
    c: Equal(g8,g4)
    c: Equal(g4,g5)
    c: PointOnObject(g4,g-1)
    c: PointOnObject(g3,g-2)
    c: PointOnObject(g2,g-1)
    c: Coincident(g15,g6)
    c: Coincident(g15,g8)
    c: Coincident(g16,g7)
    c: Coincident(g16,g5)
    c: PointOnObject(g1,g15)
    c: PointOnObject(g1,g16)
    c: Perpendicular(g16,g15)
    c: Angle(g15,g-2) = 0.785398
    c: Coincident(g17,g3)
    c: Coincident(g17,g3)
    c: Equal(g17,g13)
FEATURE [PartDesign::Pocket] Pocket010
  BaseFeature = -> Pad005
  Direction = (0,0,-1)
  Length = 12.7
  Length2 = 5
  Profile = -> Sketch016
  ReferenceAxis = -> Sketch016 [N_Axis]
  Type = 0
FEATURE [Sketcher::SketchObject] Sketch017
  FullyConstrained = true
  MapMode = 5
  Placement = pos=(0,0,15.24) rot=(0,0,1;0rad)
  Support = -> [Pocket010]
  sketch-geometry (1):
    g0: Circle CenterX=0 CenterY=0 CenterZ=0 NormalX=0 NormalY=0 NormalZ=1 AngleXU=0 Radius=2.54
  constraints (2):
    c: Coincident(g0,g-1)
    c: Diameter(g0) = 5.08
FEATURE [PartDesign::Pocket] Pocket011
  BaseFeature = -> Pocket010
  Direction = (0,0,-1)
  Length = 5
  Length2 = 5
  Profile = -> Sketch017
  ReferenceAxis = -> Sketch017 [N_Axis]
  Type = 1
FEATURE [PartDesign::CoordinateSystem] Local_CS009  label="MotorShaftMount"
  AttacherType = Attacher::AttachEngine3D
  MapMode = 11
  Placement = pos=(0,0,15.24) rot=(0,0,1;1.5708rad)
  Support = -> [Pocket011]
FEATURE [PartDesign::Body] Body005  label="TimingPulley"
  Group = -> [Sketch015,Pad005,DatumPlane001,Sketch016,Pocket010,Sketch017,Pocket011,Local_CS009]
  Origin = -> Origin006
  Tip = -> Pocket011
FEATURE [App::Link] TimingPulley  label="TimingPulley001"
  AssemblyType = Part::Link
  AttachedBy = #Local_CS009
  AttachedTo = NEMA17#Local_CS010
  LinkPlacement = pos=(444.5,6.14,558.8) rot=(-0.862856,0.357407,-0.357407;4.56541rad)
  LinkedObject = -> Body005
  Placement = pos=(444.5,6.14,558.8) rot=(-0.862856,0.357407,-0.357407;4.56541rad)
  SolverId = Asm4EE
  expr: Placement = NEMA17.Placement * Local_CS010.Placement * AttachmentOffset * Local_CS009.Placement ^ -1
FEATURE [PartDesign::CoordinateSystem] Local_CS011  label="UpperRail"
  AttacherType = Attacher::AttachEngine3D
  MapMode = 11
  Placement = pos=(-12.7,0,584.2) rot=(0.707107,0,0.707107;3.14159rad)
  Support = -> [Pocket009]
FEATURE [PartDesign::CoordinateSystem] Local_CS012  label="LowerRail"
  AttacherType = Attacher::AttachEngine3D
  MapMode = 11
  Placement = pos=(-12.7,0,533.4) rot=(0.707107,0,0.707107;3.14159rad)
  Support = -> [Pocket009]
FEATURE [Sketcher::SketchObject] Sketch018
  FullyConstrained = true
  MapMode = 5
  Placement = pos=(0,0,0) rot=(0.57735,0.57735,0.57735;2.0944rad)
  Support = -> [YZ_Plane007]
  sketch-geometry (1):
    g0: Circle CenterX=0 CenterY=0 CenterZ=0 NormalX=0 NormalY=0 NormalZ=1 AngleXU=0 Radius=4
  constraints (2):
    c: Coincident(g0,g-1)
    c: Diameter(g0) = 8
FEATURE [PartDesign::Pad] Pad006
  Direction = (1,-2e-16,3e-16)
  Length = 914.4
  Length2 = 10
  Midplane = true
  Placement = pos=(0,0,0) rot=(0.57735,0.57735,0.57735;2.0944rad)
  Profile = -> Sketch018
  ReferenceAxis = -> Sketch018 [N_Axis]
  Type = 0
FEATURE [PartDesign::CoordinateSystem] Local_CS013  label="Mount"
  AttacherType = Attacher::AttachEngine3D
  MapMode = 11
  Placement = pos=(-457.2,2.034e-13,-1.27e-13) rot=(0.707107,0,0.707107;3.14159rad)
  Support = -> [Pad006]
FEATURE [PartDesign::Body] Body006  label="Rail"
  Group = -> [Sketch018,Pad006,Local_CS013]
  Origin = -> Origin007
  Tip = -> Pad006
FEATURE [App::Link] Rail  label="Rail001"
  AssemblyType = Part::Link
  AttachedBy = #Local_CS013
  AttachedTo = Endplate_Extrusion#Local_CS011
  LinkPlacement = pos=(1.40403e-11,-8.7626e-12,584.2) rot=(0,0,1;0rad)
  LinkedObject = -> Body006
  Placement = pos=(1.40403e-11,-8.7626e-12,584.2) rot=(0,0,1;0rad)
  SolverId = Asm4EE
  expr: Placement = Endplate_Extrusion.Placement * Local_CS011.Placement * AttachmentOffset * Local_CS013.Placement ^ -1
FEATURE [App::Link] Rail_2
  AssemblyType = Part::Link
  AttachedBy = #Local_CS013
  AttachedTo = Endplate_Extrusion#Local_CS012
  LinkPlacement = pos=(1.27898e-11,-8.3537e-12,533.4) rot=(0,0,1;0rad)
  LinkedObject = -> Body006
  Placement = pos=(1.27898e-11,-8.3537e-12,533.4) rot=(0,0,1;0rad)
  SolverId = Asm4EE
  expr: Placement = Endplate_Extrusion.Placement * Local_CS012.Placement * AttachmentOffset * Local_CS013.Placement ^ -1
FEATURE [Sketcher::SketchObject] Sketch019
  FullyConstrained = true
  MapMode = 5
  Placement = pos=(0,0,0) rot=(1,0,0;1.5708rad)
  Support = -> [XZ_Plane008]
  sketch-geometry (2):
    g0: Circle CenterX=0 CenterY=0 CenterZ=0 NormalX=0 NormalY=0 NormalZ=1 AngleXU=0 Radius=2.5
    g1: Circle CenterX=-0.762 CenterY=0 CenterZ=0 NormalX=0 NormalY=0 NormalZ=1 AngleXU=0 Radius=3.5
  constraints (5):
    c: Coincident(g0,g-1)
    c: PointOnObject(g1,g-1)
    c: Diameter(g0) = 5
    c: Diameter(g1) = 7
    c: Distance(g1,g0) = 0.762
FEATURE [PartDesign::Pad] Pad007
  Direction = (0,-1,2e-16)
  Length = 12.7
  Length2 = 10
  Placement = pos=(0,0,0) rot=(1,0,0;1.5708rad)
  Profile = -> Sketch019
  ReferenceAxis = -> Sketch019 [N_Axis]
  Type = 0
FEATURE [PartDesign::CoordinateSystem] Local_CS014
  AttacherType = Attacher::AttachEngine3D
  MapMode = 11
  Placement = pos=(0,0,0) rot=(0.57735,-0.57735,0.57735;2.0944rad)
  Support = -> [Pad007]
FEATURE [PartDesign::Body] Body007  label="Eccentric"
  Group = -> [Sketch019,Pad007,Local_CS014]
  Origin = -> Origin008
  Tip = -> Pad007
FEATURE [Part::Feature] Part__Feature  label="NEA17"
  shape: bbox 42.63 x 42.63 x 55.3 mm, 174 faces (baked)
FEATURE [PartDesign::FeatureBase] BaseFeature
  BaseFeature = -> Part__Feature
FEATURE [PartDesign::CoordinateSystem] Local_CS008
  AttacherType = Attacher::AttachEngine3D
  AttachmentOffset = pos=(0,0,0) rot=(0,0,1;0.785398rad)
  MapMode = 11
  Placement = pos=(-4.7,-15,1066) rot=(0.92388,-0.382683,0;3.14159rad)
  Support = -> [BaseFeature]
FEATURE [PartDesign::CoordinateSystem] Local_CS010  label="SprocketMount"
  AttacherType = Attacher::AttachEngine3D
  MapMode = 11
  Placement = pos=(-4.7,-15,1044.2) rot=(0.707107,-0.707107,0;3.14159rad)
  Support = -> [BaseFeature]
FEATURE [PartDesign::Body] Body004  label="NEMA17"
  BaseFeature = -> Part__Feature
  Group = -> [BaseFeature,Local_CS008,Local_CS010]
  Origin = -> Origin005
  Tip = -> BaseFeature
FEATURE [PartDesign::CoordinateSystem] Local_CS015  label="Eccentric001"
  AttacherType = Attacher::AttachEngine3D
  MapMode = 11
  Placement = pos=(0,9.525,558.8) rot=(0.57735,-0.57735,0.57735;2.0944rad)
  Support = -> [Pocket009]
FEATURE [PartDesign::Body] Body002  label="Endplate Extrusion"
  Group = -> [Sketch005,Pad002,Sketch006,Pocket003,Sketch007,Pocket004,Local_CS004,Sketch011,Pocket007,Sketch012,Pocket008,Sketch013,Pocket009,Local_CS011,Local_CS012,Local_CS015]
  Origin = -> Origin002
  Tip = -> Pocket009
FEATURE [App::Link] Eccentric  label="Eccentric002"
  AssemblyType = Part::Link
  AttachedBy = #Local_CS014
  AttachedTo = Endplate_Extrusion#Local_CS015
  LinkPlacement = pos=(-444.5,9.525,558.8) rot=(0,0,1;0rad)
  LinkedObject = -> Body007
  Placement = pos=(-444.5,9.525,558.8) rot=(0,0,1;0rad)
  SolverId = Asm4EE
  expr: Placement = Endplate_Extrusion.Placement * Local_CS015.Placement * AttachmentOffset * Local_CS014.Placement ^ -1
FEATURE [App::Part] Model  label="Frame Assembly"
  AssemblyType = Part::Link
  Group = -> [LCS_Origin,Constraints,Variables,Configurations,Lower_Extrusion,Motor_Extrusion,Endplate_Extrusion,NEMA17,TimingPulley,Rail,Rail_2,Eccentric]
  Origin = -> Origin004
  Type = Assembly
FEATURE [Sketcher::SketchObject] Sketch020
  ExternalGeometry = -> [Pad004]
  FullyConstrained = true
  MapMode = 5
  Placement = pos=(0,-12.7,0) rot=(1,0,0;1.5708rad)
  Support = -> [Pad004]
  sketch-geometry (2):
    g0: Circle CenterX=0 CenterY=536.88 CenterZ=0 NormalX=0 NormalY=0 NormalZ=1 AngleXU=0 Radius=3.302
    g1: Circle CenterX=0 CenterY=580.72 CenterZ=0 NormalX=0 NormalY=0 NormalZ=1 AngleXU=0 Radius=3.302
  constraints (4):
    c: Coincident(g0,g-5)
    c: Coincident(g1,g-3)
    c: Equal(g1,g0)
    c: Diameter(g1) = 6.604
FEATURE [PartDesign::Pocket] Pocket012
  BaseFeature = -> Pad004
  Direction = (0,1,-2e-16)
  Length = 7.62
  Length2 = 5
  Profile = -> Sketch020
  ReferenceAxis = -> Sketch020 [N_Axis]
  Type = 0
FEATURE [Sketcher::SketchObject] Sketch021
  ExternalGeometry = -> [Pocket012]
  FullyConstrained = true
  MapMode = 5
  Placement = pos=(9.525,0,0) rot=(0.57735,0.57735,0.57735;2.0944rad)
  Support = -> [Pocket012]
  sketch-geometry (4):
    g0: LineSegment StartX=-42.734 StartY=5.46332 StartZ=0 EndX=-28.1652 EndY=26.2698 EndZ=0
    g1: LineSegment StartX=42.734 StartY=5.46332 StartZ=0 EndX=28.1652 EndY=26.2698 EndZ=0
    g2: Circle CenterX=-28.1652 CenterY=26.2698 CenterZ=0 NormalX=0 NormalY=0 NormalZ=1 AngleXU=0 Radius=3.175
    g3: Circle CenterX=28.1652 CenterY=26.2698 CenterZ=0 NormalX=0 NormalY=0 NormalZ=1 AngleXU=0 Radius=3.175
  constraints (10):
    c: Symmetric(g-3,g-3,g0)
    c: Symmetric(g-4,g-4,g1)
    c: Equal(g0,g1)
    c: Perpendicular(g-3,g0)
    c: Perpendicular(g-4,g1)
    c: Distance(g1) = 25.4
    c: Coincident(g2,g0)
    c: Coincident(g3,g1)
    c: Equal(g3,g2)
    c: Diameter(g2) = 6.35
FEATURE [PartDesign::Pocket] Pocket013
  BaseFeature = -> Pocket012
  Direction = (-1,0,0)
  Length = 5
  Length2 = 5
  Profile = -> Sketch021
  ReferenceAxis = -> Sketch021 [N_Axis]
  Type = 1
FEATURE [PartDesign::Body] Body001  label="Motor Extrusion"
  Group = -> [Sketch001,Pad001,Sketch002,Pocket,Sketch003,Pocket001,Sketch004,Pocket002,Local_CS,Local_CS001,Local_CS002,Local_CS003,Sketch010,Pocket006,DatumPlane,Sketch014,Pad004,Sketch020,Pocket012,Sketch021,Pocket013]
  Origin = -> Origin001
  Tip = -> Pocket013
FEATURE [TechDraw::DrawSVGTemplate] Template
  EditableTexts = Designed_by_Name=Team AJMK; Drawing_number=v1.1-20-g11b148a; FC-Date=March 2023; FC-SC=N/A; FC-SH=Sheet; FC-Title=Pendulum Frame Notes; Subtitle=EG-310; Weight=40lb
  Height = 210
  Orientation = 1
  Width = 297
FEATURE [TechDraw::DrawProjGroupItem] ProjItem  label="Front"
  CoarseView = false
  Direction = (0,-1,0)
  Focus = 100
  HardHidden = false
  IsoCount = 0
  IsoHidden = false
  IsoVisible = false
  LockPosition = true
  Perspective = false
  Rotation = 0
  RotationVector = (1,0,0)
  Scale = 0.125
  ScaleType = 2
  SeamHidden = false
  SeamVisible = true
  SmoothHidden = false
  SmoothVisible = true
  Source = -> [Model]
  Type = 0
  X = 0
  XDirection = (1,0,0)
  Y = 0
FEATURE [TechDraw::DrawProjGroupItem] ProjItem001  label="Left"
  CoarseView = false
  Direction = (-1,-1e-16,0)
  Focus = 100
  HardHidden = false
  IsoCount = 0
  IsoHidden = false
  IsoVisible = false
  LockPosition = true
  Perspective = false
  Rotation = 0
  RotationVector = (1,0,0)
  ScaleType = 2
  SeamHidden = false
  SeamVisible = true
  SmoothHidden = false
  SmoothVisible = true
  Source = -> [Model]
  Type = 1
  X = 73.2604
  XDirection = (1e-16,-1,0)
  Y = 0
FEATURE [TechDraw::DrawProjGroup] ProjGroup
  Anchor = -> ProjItem
  AutoDistribute = true
  LockPosition = false
  ProjectionType = 0
  Rotation = 0
  Scale = 0.125
  ScaleType = 2
  Source = -> [Model]
  Views = -> [ProjItem,ProjItem001]
  X = 76.9612
  Y = 151.382
  spacingX = 15.0114
  spacingY = 15.0114
FEATURE [TechDraw::DrawViewDetail] Detail
  AnchorPoint = (-25.1968,-270.84,0)
  BaseView = -> ProjItem001
  CoarseView = false
  Direction = (-1,-1e-16,0)
  Focus = 100
  HardHidden = false
  IsoCount = 0
  IsoHidden = false
  IsoVisible = false
  LockPosition = false
  Perspective = false
  Radius = 44.45
  Reference = 1
  Rotation = 0
  ScaleType = 2
  SeamHidden = false
  SeamVisible = true
  SmoothHidden = false
  SmoothVisible = true
  Source = -> [Model]
  X = 233.17
  XDirection = (1e-16,-1,0)
  Y = 151.309
FEATURE [TechDraw::DrawViewDimension] Dimension002
  AngleOverride = false
  Arbitrary = false
  ArbitraryTolerances = false
  EqualTolerance = true
  ExtensionAngle = 0
  FormatSpec = %.3f
  FormatSpecOverTolerance = %+.3f
  FormatSpecUnderTolerance = %+.3f
  Inverted = false
  LineAngle = 0
  LockPosition = false
  MeasureType = 1
  OverTolerance = 0
  References2D = -> [ProjItem]
  Rotation = 0
  ScaleType = 0
  TheoreticalExact = false
  Type = 1
  UnderTolerance = 0
  X = -1.09679
  Y = -41.0453
FEATURE [TechDraw::DrawViewDimension] Dimension003
  AngleOverride = false
  Arbitrary = false
  ArbitraryTolerances = false
  EqualTolerance = true
  ExtensionAngle = 0
  FormatSpec = %.3f
  FormatSpecOverTolerance = %+.3f
  FormatSpecUnderTolerance = %+.3f
  Inverted = false
  LineAngle = 0
  LockPosition = false
  MeasureType = 1
  OverTolerance = 0
  References2D = -> [ProjItem]
  Rotation = 0
  ScaleType = 0
  TheoreticalExact = false
  Type = 2
  UnderTolerance = 0
  X = -62.8864
  Y = 1.52182
FEATURE [TechDraw::DrawViewDimension] Dimension004
  AngleOverride = false
  Arbitrary = false
  ArbitraryTolerances = false
  EqualTolerance = true
  ExtensionAngle = 0
  FormatSpec = %.3f
  FormatSpecOverTolerance = %+.3f
  FormatSpecUnderTolerance = %+.3f
  Inverted = false
  LineAngle = 0
  LockPosition = false
  MeasureType = 1
  OverTolerance = 0
  References2D = -> [ProjItem]
  Rotation = 0
  ScaleType = 0
  TheoreticalExact = false
  Type = 6
  UnderTolerance = 0
  X = -33.8328
  Y = -26.3581
FEATURE [TechDraw::DrawViewAnnotation] Annotation
  Font = osifont
  LineSpace = 80
  LockPosition = false
  MaxWidth = -1
  Rotation = 0
  ScaleType = 0
  Text = These drawings are not | intended to be used for | final machining. | They are provided for general | assembly and visualization. | Assume all measurements are | saw-cut or best effort.
  TextSize = 5.0038
  TextStyle = 0
  X = 53.3222
  Y = 60.8754
FEATURE [TechDraw::DrawViewDimension] Dimension
  AngleOverride = false
  Arbitrary = false
  ArbitraryTolerances = false
  EqualTolerance = true
  ExtensionAngle = 0
  FormatSpec = %.3f
  FormatSpecOverTolerance = %+.3f
  FormatSpecUnderTolerance = %+.3f
  Inverted = false
  LineAngle = 0
  LockPosition = false
  MeasureType = 1
  OverTolerance = 0
  References2D = -> [Detail]
  Rotation = 0
  ScaleType = 0
  TheoreticalExact = false
  Type = 0
  UnderTolerance = 0
  X = -15.2512
  Y = 11.3953
FEATURE [TechDraw::DrawViewDimension] Dimension005
  AngleOverride = false
  Arbitrary = false
  ArbitraryTolerances = false
  EqualTolerance = true
  ExtensionAngle = 0
  FormatSpec = %.3f
  FormatSpecOverTolerance = %+.3f
  FormatSpecUnderTolerance = %+.3f
  Inverted = false
  LineAngle = 0
  LockPosition = false
  MeasureType = 1
  OverTolerance = 0
  References2D = -> [Detail]
  Rotation = 0
  ScaleType = 0
  TheoreticalExact = false
  Type = 0
  UnderTolerance = 0
  X = -22.3356
  Y = -7.89442
FEATURE [TechDraw::DrawViewDimension] Dimension006
  AngleOverride = false
  Arbitrary = false
  ArbitraryTolerances = false
  EqualTolerance = true
  ExtensionAngle = 0
  FormatSpec = %.3f
  FormatSpecOverTolerance = %+.3f
  FormatSpecUnderTolerance = %+.3f
  Inverted = false
  LineAngle = 0
  LockPosition = false
  MeasureType = 1
  OverTolerance = 0
  References2D = -> [Detail]
  Rotation = 0
  ScaleType = 0
  TheoreticalExact = false
  Type = 6
  UnderTolerance = 0
  X = 5.8865
  Y = 11.3083
FEATURE [TechDraw::DrawPage] Page  label="General Assembly"
  KeepUpdated = true
  NextBalloonIndex = 1
  ProjectionType = 0
  Template = -> Template
  Views = -> [ProjGroup,Detail,Dimension002,Dimension003,Dimension004,Annotation,Dimension,Dimension005,Dimension006]
FEATURE [Sketcher::SketchObject] Sketch022
  FullyConstrained = true
  MapMode = 5
  Placement = pos=(0,0,0) rot=(0.57735,0.57735,0.57735;2.0944rad)
  Support = -> [YZ_Plane009]
  sketch-geometry (4):
    g0: LineSegment StartX=-73.025 StartY=0 StartZ=0 EndX=73.025 EndY=0 EndZ=0
    g1: LineSegment StartX=73.025 StartY=0 StartZ=0 EndX=50.8 EndY=80.9625 EndZ=0
    g2: LineSegment StartX=50.8 StartY=80.9625 StartZ=0 EndX=-50.8 EndY=80.9625 EndZ=0
    g3: LineSegment StartX=-50.8 StartY=80.9625 StartZ=0 EndX=-73.025 EndY=0 EndZ=0
  constraints (10):
    c: PointOnObject(g0,g-1)
    c: Coincident(g1,g0)
    c: Coincident(g2,g1)
    c: Coincident(g3,g2)
    c: Coincident(g3,g0)
    c: Symmetric(g0,g0,g-2)
    c: Symmetric(g1,g2,g-2)
    c: Distance(g1,g0) = 80.9625
    c: Distance(g2) = 101.6
    c: Distance(g0) = 146.05
FEATURE [PartDesign::Pad] Pad008
  Direction = (1,-2e-16,3e-16)
  Length = 4
  Length2 = 10
  Placement = pos=(0,0,0) rot=(0.57735,0.57735,0.57735;2.0944rad)
  Profile = -> Sketch022
  ReferenceAxis = -> Sketch022 [N_Axis]
  Type = 0
FEATURE [Sketcher::SketchObject] Sketch023
  FullyConstrained = true
  MapMode = 5
  Support = -> [XY_Plane010]
  sketch-geometry (5):
    g0: LineSegment StartX=-431.8 StartY=73.025 StartZ=0 EndX=-431.8 EndY=-73.025 EndZ=0
    g1: LineSegment StartX=-431.8 StartY=-73.025 StartZ=0 EndX=431.8 EndY=-73.025 EndZ=0
    g2: LineSegment StartX=431.8 StartY=-73.025 StartZ=0 EndX=431.8 EndY=73.025 EndZ=0
    g3: LineSegment StartX=431.8 StartY=73.025 StartZ=0 EndX=-431.8 EndY=73.025 EndZ=0
    g4: GeomPoint X=0 Y=0 Z=0
  constraints (12):
    c: Coincident(g0,g1)
    c: Coincident(g1,g2)
    c: Coincident(g2,g3)
    c: Coincident(g3,g0)
    c: Horizontal(g1)
    c: Horizontal(g3)
    c: Vertical(g0)
    c: Vertical(g2)
    c: Symmetric(g1,g0,g4)
    c: Coincident(g4,g-1)
    c: Distance(g2) = 146.05
    c: Distance(g1) = 863.6
FEATURE [PartDesign::Pad] Pad009
  Direction = (0,0,1)
  Length = 3.9878
  Length2 = 10
  Profile = -> Sketch023
  ReferenceAxis = -> Sketch023 [N_Axis]
  Reversed = true
  Type = 0
FEATURE [Sketcher::SketchObject] Sketch024
  FullyConstrained = true
  MapMode = 5
  Support = -> [XY_Plane011]
  sketch-geometry (13):
    g0: LineSegment StartX=-457.2 StartY=50.8 StartZ=0 EndX=457.2 EndY=50.8 EndZ=0
    g1: LineSegment StartX=457.2 StartY=-50.8 StartZ=0 EndX=-457.2 EndY=-50.8 EndZ=0
    g2: GeomPoint X=0 Y=-1e-16 Z=0
    g3: LineSegment StartX=457.2 StartY=50.8 StartZ=0 EndX=457.2 EndY=12.7 EndZ=0
    g4: LineSegment StartX=457.2 StartY=12.7 StartZ=0 EndX=431.8 EndY=12.7 EndZ=0
    g5: LineSegment StartX=431.8 StartY=12.7 StartZ=0 EndX=431.8 EndY=-12.7 EndZ=0
    g6: LineSegment StartX=431.8 StartY=-12.7 StartZ=0 EndX=457.2 EndY=-12.7 EndZ=0
    g7: LineSegment StartX=457.2 StartY=-12.7 StartZ=0 EndX=457.2 EndY=-50.8 EndZ=0
    g8: LineSegment StartX=-457.2 StartY=50.8 StartZ=0 EndX=-457.2 EndY=12.7 EndZ=0
    g9: LineSegment StartX=-457.2 StartY=12.7 StartZ=0 EndX=-431.8 EndY=12.7 EndZ=0
    g10: LineSegment StartX=-431.8 StartY=12.7 StartZ=0 EndX=-431.8 EndY=-12.7 EndZ=0
    g11: LineSegment StartX=-431.8 StartY=-12.7 StartZ=0 EndX=-457.2 EndY=-12.7 EndZ=0
    g12: LineSegment StartX=-457.2 StartY=-12.7 StartZ=0 EndX=-457.2 EndY=-50.8 EndZ=0
  constraints (34):
    c: Horizontal(g0)
    c: Horizontal(g1)
    c: Symmetric(g0,g1,g2)
    c: Coincident(g2,g-1)
    c: Distance(g0) = 914.4
    c: Coincident(g3,g0)
    c: Vertical(g3)
    c: Coincident(g4,g3)
    c: Horizontal(g4)
    c: Coincident(g5,g4)
    c: Vertical(g5)
    c: Coincident(g6,g5)
    c: Horizontal(g6)
    c: Coincident(g7,g6)
    c: Coincident(g7,g1)
    c: Coincident(g8,g0)
    c: Vertical(g8)
    c: Coincident(g9,g8)
    c: Horizontal(g9)
    c: Coincident(g10,g9)
    c: Vertical(g10)
    c: Coincident(g11,g10)
    c: Horizontal(g11)
    c: Coincident(g12,g11)
    c: Coincident(g12,g1)
    c: Tangent(g12,g8)
    c: Tangent(g3,g7)
    c: Equal(g4,g5)
    c: Equal(g6,g9)
    c: Equal(g9,g10)
    c: Equal(g12,g8)
    c: Equal(g8,g3)
    c: Distance(g4) = 25.4
    c: Distance(g0,g1) = 101.6
FEATURE [PartDesign::Pad] Pad010
  Direction = (0,0,1)
  Length = 4
  Length2 = 10
  Profile = -> Sketch024
  ReferenceAxis = -> Sketch024 [N_Axis]
  Type = 0
FEATURE [PartDesign::Body] Body010  label="TopPanel"
  Group = -> [Sketch024,Pad010]
  Origin = -> Origin011
  Placement = pos=(0,0,72.7001) rot=(0,0,1;0rad)
  Tip = -> Pad010
FEATURE [Sketcher::SketchObject] Sketch025
  FullyConstrained = true
  MapMode = 5
  Placement = pos=(0,0,0) rot=(1,0,0;1.5708rad)
  Support = -> [XZ_Plane012]
  sketch-geometry (5):
    g0: LineSegment StartX=-461.2 StartY=-36.576 StartZ=0 EndX=-461.2 EndY=36.576 EndZ=0
    g1: LineSegment StartX=-461.2 StartY=36.576 StartZ=0 EndX=461.2 EndY=36.576 EndZ=0
    g2: LineSegment StartX=461.2 StartY=36.576 StartZ=0 EndX=461.2 EndY=-36.576 EndZ=0
    g3: LineSegment StartX=461.2 StartY=-36.576 StartZ=0 EndX=-461.2 EndY=-36.576 EndZ=0
    g4: GeomPoint X=0 Y=0 Z=0
  constraints (12):
    c: Coincident(g0,g1)
    c: Coincident(g1,g2)
    c: Coincident(g2,g3)
    c: Coincident(g3,g0)
    c: Horizontal(g1)
    c: Horizontal(g3)
    c: Vertical(g0)
    c: Vertical(g2)
    c: Symmetric(g1,g0,g4)
    c: Coincident(g4,g-1)
    c: Distance(g1) = 922.4
    c: Distance(g0) = 73.152
FEATURE [PartDesign::Pad] Pad011
  Direction = (0,-1,2e-16)
  Length = 4
  Length2 = 10
  Placement = pos=(0,0,0) rot=(1,0,0;1.5708rad)
  Profile = -> Sketch025
  ReferenceAxis = -> Sketch025 [N_Axis]
  Type = 0
FEATURE [PartDesign::Body] Body011  label="FacePanel"
  Group = -> [Sketch025,Pad011]
  Origin = -> Origin012
  Placement = pos=(0,-62.0274,34.8655) rot=(-1,0,0;0.314159rad)
  Tip = -> Pad011
FEATURE [Sketcher::SketchObject] Sketch026
  ExternalGeometry = -> [Pad008]
  FullyConstrained = true
  MapMode = 5
  Placement = pos=(4,-9e-16,9e-16) rot=(0.57735,0.57735,0.57735;2.0944rad)
  Support = -> [Pad008]
  sketch-geometry (2):
    g0: Circle CenterX=0 CenterY=61.1378 CenterZ=0 NormalX=0 NormalY=0 NormalZ=1 AngleXU=0 Radius=3.175
    g1: Circle CenterX=0 CenterY=23.0378 CenterZ=0 NormalX=0 NormalY=0 NormalZ=1 AngleXU=0 Radius=3.175
  constraints (6):
    c: PointOnObject(g0,g-2)
    c: PointOnObject(g1,g-2)
    c: Equal(g1,g0)
    c: Diameter(g0) = 6.35
    c: Distance(g0,g1) = 38.1
    c: Distance(g0,g-3) = 19.8247
FEATURE [PartDesign::Pocket] Pocket014
  BaseFeature = -> Pad008
  Direction = (-1,4e-16,-4e-16)
  Length = 5.0038
  Length2 = 5
  Placement = pos=(0,0,0) rot=(0.57735,0.57735,0.57735;2.0944rad)
  Profile = -> Sketch026
  ReferenceAxis = -> Sketch026 [N_Axis]
  Type = 0
FEATURE [PartDesign::Body] Body008  label="Endplate"
  Group = -> [Sketch022,Pad008,Sketch026,Pocket014]
  Origin = -> Origin009
  Placement = pos=(457.342,0,-3.95554) rot=(0,0,1;0rad)
  Tip = -> Pocket014
FEATURE [Sketcher::SketchObject] Sketch027
  FullyConstrained = true
  MapMode = 5
  Placement = pos=(0,0,-3.9878) rot=(1,0,0;3.14159rad)
  Support = -> [Pad009]
  sketch-geometry (5):
    g0: LineSegment StartX=0 StartY=0 StartZ=0 EndX=-355.6 EndY=0 EndZ=0
    g1: LineSegment StartX=0 StartY=0 StartZ=0 EndX=355.6 EndY=0 EndZ=0
    g2: Circle CenterX=-355.6 CenterY=0 CenterZ=0 NormalX=0 NormalY=0 NormalZ=1 AngleXU=0 Radius=3.175
    g3: Circle CenterX=0 CenterY=0 CenterZ=0 NormalX=0 NormalY=0 NormalZ=1 AngleXU=0 Radius=3.175
    g4: Circle CenterX=355.6 CenterY=0 CenterZ=0 NormalX=0 NormalY=0 NormalZ=1 AngleXU=0 Radius=3.175
  constraints (12):
    c: Coincident(g0,g-1)
    c: Horizontal(g0)
    c: Coincident(g1,g0)
    c: PointOnObject(g1,g-1)
    c: Equal(g1,g0)
    c: Coincident(g2,g0)
    c: Coincident(g3,g0)
    c: Coincident(g4,g1)
    c: Equal(g4,g3)
    c: Equal(g3,g2)
    c: Diameter(g2) = 6.35
    c: Distance(g0) = 355.6
FEATURE [PartDesign::Pocket] Pocket015
  BaseFeature = -> Pad009
  Direction = (0,0,1)
  Length = 5
  Length2 = 5
  Profile = -> Sketch027
  ReferenceAxis = -> Sketch027 [N_Axis]
  Type = 1
FEATURE [PartDesign::Body] Body009  label="BottomPanel"
  Group = -> [Sketch023,Pad009,Sketch027,Pocket015]
  Origin = -> Origin010
  Tip = -> Pocket015
FEATURE [TechDraw::DrawSVGTemplate] Template001
  EditableTexts = Designed_by_Name=Team AJMK; Drawing_number=v1.1-24-g9a9eebf; FC-Date=Today; FC-SC=Cust; FC-SH=1 of 1; FC-Title=Panel Assembly; Subtitle=EG-310 SNHU; Weight=1lb
  Height = 210
  Orientation = 1
  Template = <path>
  Width = 297
FEATURE [TechDraw::DrawViewPart] View001
  Caption = Side Panel
  CoarseView = false
  Direction = (1,0,0)
  Focus = 100
  HardHidden = false
  IsoCount = 0
  IsoHidden = false
  IsoVisible = false
  LockPosition = false
  Perspective = false
  Rotation = 0
  ScaleType = 0
  SeamHidden = false
  SeamVisible = true
  SmoothHidden = false
  SmoothVisible = true
  Source = -> [Pocket014]
  X = 88.6002
  XDirection = (0,1,-1.19209e-07)
  Y = 146.538
FEATURE [TechDraw::DrawViewPart] View002
  Caption = Bottom Panel
  CoarseView = false
  Direction = (0,0,-1)
  Focus = 100
  HardHidden = false
  IsoCount = 0
  IsoHidden = false
  IsoVisible = false
  LockPosition = false
  Perspective = false
  Rotation = 0
  Scale = 0.15
  ScaleType = 2
  SeamHidden = false
  SeamVisible = true
  SmoothHidden = false
  SmoothVisible = true
  Source = -> [Pocket015]
  X = 80.1552
  XDirection = (1,-1.19209e-07,0)
  Y = 74.4254
FEATURE [TechDraw::DrawViewDimension] Dimension007
  AngleOverride = false
  Arbitrary = false
  ArbitraryTolerances = false
  EqualTolerance = true
  ExtensionAngle = 0
  FormatSpec = %.3f
  FormatSpecOverTolerance = %+.3f
  FormatSpecUnderTolerance = %+.3f
  Inverted = false
  LineAngle = 0
  LockPosition = false
  MeasureType = 1
  OverTolerance = 0
  References2D = -> [View001]
  Rotation = 0
  ScaleType = 0
  TheoreticalExact = false
  Type = 2
  UnderTolerance = 0
  X = 41.9216
  Y = 1.92757
FEATURE [TechDraw::DrawViewDimension] Dimension008
  AngleOverride = false
  Arbitrary = false
  ArbitraryTolerances = false
  EqualTolerance = true
  ExtensionAngle = 0
  FormatSpec = %.3f
  FormatSpecOverTolerance = %+.3f
  FormatSpecUnderTolerance = %+.3f
  Inverted = false
  LineAngle = 0
  LockPosition = false
  MeasureType = 1
  OverTolerance = 0
  References2D = -> [View001]
  Rotation = 0
  ScaleType = 0
  TheoreticalExact = false
  Type = 1
  UnderTolerance = 0
  X = -0.605346
  Y = -28.1368
FEATURE [TechDraw::DrawViewDimension] Dimension009
  AngleOverride = false
  Arbitrary = false
  ArbitraryTolerances = false
  EqualTolerance = true
  ExtensionAngle = 0
  FormatSpec = %.3f
  FormatSpecOverTolerance = %+.3f
  FormatSpecUnderTolerance = %+.3f
  Inverted = false
  LineAngle = 0
  LockPosition = false
  MeasureType = 1
  OverTolerance = 0
  References2D = -> [View001]
  Rotation = 0
  ScaleType = 0
  TheoreticalExact = false
  Type = 1
  UnderTolerance = 0
  X = -66.3185
  Y = 47.5275
FEATURE [TechDraw::DrawViewDimension] Dimension010
  AngleOverride = false
  Arbitrary = false
  ArbitraryTolerances = false
  EqualTolerance = true
  ExtensionAngle = 0
  FormatSpec = %.3f
  FormatSpecOverTolerance = %+.3f
  FormatSpecUnderTolerance = %+.3f
  Inverted = false
  LineAngle = 0
  LockPosition = false
  MeasureType = 1
  OverTolerance = 0
  References2D = -> [View001]
  Rotation = 0
  ScaleType = 0
  TheoreticalExact = false
  Type = 2
  UnderTolerance = 0
  X = -14.3265
  Y = 31.8972
FEATURE [TechDraw::DrawViewDimension] Dimension011
  AngleOverride = false
  Arbitrary = false
  ArbitraryTolerances = false
  EqualTolerance = true
  ExtensionAngle = 0
  FormatSpec = %.3f
  FormatSpecOverTolerance = %+.3f
  FormatSpecUnderTolerance = %+.3f
  Inverted = false
  LineAngle = 0
  LockPosition = false
  MeasureType = 1
  OverTolerance = 0
  References2D = -> [View001]
  Rotation = 0
  ScaleType = 0
  TheoreticalExact = false
  Type = 2
  UnderTolerance = 0
  X = 6.45702
  Y = 12.6454
FEATURE [TechDraw::DrawViewDimension] Dimension012
  AngleOverride = false
  Arbitrary = false
  ArbitraryTolerances = false
  EqualTolerance = true
  ExtensionAngle = 0
  FormatSpec = %.3f
  FormatSpecOverTolerance = %+.3f
  FormatSpecUnderTolerance = %+.3f
  Inverted = false
  LineAngle = 0
  LockPosition = false
  MeasureType = 1
  OverTolerance = 0
  References2D = -> [View002]
  Rotation = 0
  ScaleType = 0
  TheoreticalExact = false
  Type = 0
  UnderTolerance = 0
  X = -58.8409
  Y = 1.02833
FEATURE [TechDraw::DrawViewDimension] Dimension013
  AngleOverride = false
  Arbitrary = false
  ArbitraryTolerances = false
  EqualTolerance = true
  ExtensionAngle = 0
  FormatSpec = %.3f
  FormatSpecOverTolerance = %+.3f
  FormatSpecUnderTolerance = %+.3f
  Inverted = false
  LineAngle = 0
  LockPosition = false
  MeasureType = 1
  OverTolerance = 0
  References2D = -> [View002]
  Rotation = 0
  ScaleType = 0
  TheoreticalExact = false
  Type = 0
  UnderTolerance = 0
  X = -32.6783
  Y = -0.895724
FEATURE [TechDraw::DrawViewDimension] Dimension014
  AngleOverride = false
  Arbitrary = false
  ArbitraryTolerances = false
  EqualTolerance = true
  ExtensionAngle = 0
  FormatSpec = %.3f
  FormatSpecOverTolerance = %+.3f
  FormatSpecUnderTolerance = %+.3f
  Inverted = false
  LineAngle = 0
  LockPosition = false
  MeasureType = 1
  OverTolerance = 0
  References2D = -> [View002]
  Rotation = 0
  ScaleType = 0
  TheoreticalExact = false
  Type = 0
  UnderTolerance = 0
  X = 7.23146
  Y = -5.23566
FEATURE [TechDraw::DrawViewDimension] Dimension015
  AngleOverride = false
  Arbitrary = false
  ArbitraryTolerances = false
  EqualTolerance = true
  ExtensionAngle = 0
  FormatSpec = %.3f
  FormatSpecOverTolerance = %+.3f
  FormatSpecUnderTolerance = %+.3f
  Inverted = false
  LineAngle = 0
  LockPosition = false
  MeasureType = 1
  OverTolerance = 0
  References2D = -> [View002]
  Rotation = 0
  ScaleType = 0
  TheoreticalExact = false
  Type = 2
  UnderTolerance = 0
  X = 71.9307
  Y = 1.88203
FEATURE [TechDraw::DrawViewDimension] Dimension016
  AngleOverride = false
  Arbitrary = false
  ArbitraryTolerances = false
  EqualTolerance = true
  ExtensionAngle = 0
  FormatSpec = %.3f
  FormatSpecOverTolerance = %+.3f
  FormatSpecUnderTolerance = %+.3f
  Inverted = false
  LineAngle = 0
  LockPosition = false
  MeasureType = 1
  OverTolerance = 0
  References2D = -> [View002]
  Rotation = 0
  ScaleType = 0
  TheoreticalExact = false
  Type = 0
  UnderTolerance = 0
  X = 54.2419
  Y = -13.3681
FEATURE [Sketcher::SketchObject] Sketch028
  FullyConstrained = true
  MapMode = 5
  Placement = pos=(0,0,0) rot=(1,0,0;1.5708rad)
  Support = -> [XZ_Plane013]
  sketch-geometry (15):
    g0: ArcOfCircle CenterX=3.175 CenterY=0 CenterZ=0 NormalX=0 NormalY=0 NormalZ=1 AngleXU=0 Radius=20.32 StartAngle=2.60295 EndAngle=3.68024
    g1: ArcOfCircle CenterX=-3.175 CenterY=0 CenterZ=0 NormalX=0 NormalY=0 NormalZ=1 AngleXU=0 Radius=20.32 StartAngle=5.74454 EndAngle=6.82183
    g2: ArcOfCircle CenterX=0 CenterY=21.9203 CenterZ=0 NormalX=0 NormalY=0 NormalZ=1 AngleXU=0 Radius=6.35 StartAngle=0.538647 EndAngle=2.60295
    g3: ArcOfCircle CenterX=0 CenterY=-21.9203 CenterZ=0 NormalX=0 NormalY=0 NormalZ=1 AngleXU=0 Radius=6.35 StartAngle=3.68024 EndAngle=5.74454
    g4: LineSegment StartX=0 StartY=21.9203 StartZ=0 EndX=-21.9203 EndY=0 EndZ=0
    g5: LineSegment StartX=-21.9203 StartY=0 StartZ=0 EndX=0 EndY=-21.9203 EndZ=0
    g6: LineSegment StartX=0 StartY=-21.9203 StartZ=0 EndX=21.9203 EndY=0 EndZ=0
    g7: LineSegment StartX=21.9203 StartY=0 StartZ=0 EndX=0 EndY=21.9203 EndZ=0
    g8: LineSegment StartX=-5.45086 StartY=25.1777 StartZ=0 EndX=-14.2678 EndY=10.4236 EndZ=0
    g9: LineSegment StartX=-14.2678 StartY=-10.4236 StartZ=0 EndX=-5.45086 EndY=-25.1777 EndZ=0
    g10: LineSegment StartX=5.45086 StartY=-25.1777 StartZ=0 EndX=14.2678 EndY=-10.4236 EndZ=0
    g11: LineSegment StartX=14.2678 StartY=10.4236 StartZ=0 EndX=5.45086 EndY=25.1777 EndZ=0
    g12: Circle CenterX=0 CenterY=21.9203 CenterZ=0 NormalX=0 NormalY=0 NormalZ=1 AngleXU=0 Radius=2.25
    g13: Circle CenterX=0 CenterY=-21.9203 CenterZ=0 NormalX=0 NormalY=0 NormalZ=1 AngleXU=0 Radius=2.25
    g14: Circle CenterX=0 CenterY=0 CenterZ=0 NormalX=0 NormalY=0 NormalZ=1 AngleXU=0 Radius=11.125
  constraints (35):
    c: PointOnObject(g0,g-1)
    c: PointOnObject(g2,g-2)
    c: PointOnObject(g3,g-2)
    c: Coincident(g4,g2)
    c: PointOnObject(g4,g-1)
    c: Coincident(g5,g4)
    c: Coincident(g5,g3)
    c: Coincident(g6,g3)
    c: Coincident(g7,g6)
    c: Coincident(g7,g2)
    c: Equal(g5,g4)
    c: Equal(g4,g7)
    c: Equal(g7,g6)
    c: Perpendicular(g6,g7)
    c: Distance(g4) = 31
    c: Tangent(g11,g2) = -1.5708
    c: Tangent(g8,g2) = -1.5708
    c: Tangent(g8,g0) = -1.5708
    c: Tangent(g9,g0) = -1.5708
    c: Tangent(g9,g3) = -1.5708
    c: Tangent(g10,g3) = -1.5708
    c: Tangent(g10,g1) = -1.5708
    c: Tangent(g11,g1) = -1.5708
    c: Symmetric(g1,g0,g-1)
    c: Coincident(g12,g2)
    c: Coincident(g13,g3)
    c: Equal(g13,g12)
    c: Diameter(g12) = 4.5
    c: Equal(g2,g3)
    c: Radius(g2) = 6.35
    c: Coincident(g14,g-1)
    c: Diameter(g14) = 22.25
    c: Equal(g1,g0)
    c: Radius(g0) = 20.32
    c: Distance(g1,g14) = 3.175
FEATURE [PartDesign::Pad] Pad012
  Direction = (0,-1,-2e-16)
  Length = 3.683
  Length2 = 10
  Placement = pos=(0,0,0) rot=(1,0,0;1.5708rad)
  Profile = -> Sketch028
  ReferenceAxis = -> Sketch028 [N_Axis]
  Type = 0
FEATURE [PartDesign::Body] Body012  label="MotorSpacer"
  Group = -> [Sketch028,Pad012]
  Origin = -> Origin013
  Tip = -> Pad012
FEATURE [Sketcher::SketchObject] Sketch029
  FullyConstrained = true
  MapMode = 5
  Placement = pos=(0,0,0) rot=(1,0,0;1.5708rad)
  Support = -> [XZ_Plane014]
  sketch-geometry (14):
    g0: Circle CenterX=-12.7 CenterY=-7.33235 CenterZ=0 NormalX=0 NormalY=0 NormalZ=1 AngleXU=0 Radius=1.778
    g1: Circle CenterX=12.7 CenterY=-7.33235 CenterZ=0 NormalX=0 NormalY=0 NormalZ=1 AngleXU=0 Radius=1.778
    g2: Circle CenterX=0 CenterY=14.6647 CenterZ=0 NormalX=0 NormalY=0 NormalZ=1 AngleXU=0 Radius=1.778
    g3: ArcOfCircle CenterX=-3e-16 CenterY=1e-16 CenterZ=0 NormalX=0 NormalY=0 NormalZ=1 AngleXU=0 Radius=25 StartAngle=3.863e-13 EndAngle=3.14159
    g4: LineSegment StartX=25 StartY=9.6576e-12 StartZ=0 EndX=25 EndY=-25.4 EndZ=0
    g5: LineSegment StartX=25 StartY=-25.4 StartZ=0 EndX=-25 EndY=-25.4 EndZ=0
    g6: LineSegment StartX=-25 StartY=-25.4 StartZ=0 EndX=-25 EndY=-2.7818e-12 EndZ=0
    g7: LineSegment StartX=0 StartY=14.6647 StartZ=0 EndX=-12.7 EndY=-7.33235 EndZ=0
    g8: LineSegment StartX=-12.7 StartY=-7.33235 StartZ=0 EndX=12.7 EndY=-7.33235 EndZ=0
    g9: LineSegment StartX=12.7 StartY=-7.33235 StartZ=0 EndX=0 EndY=14.6647 EndZ=0
    g10: LineSegment StartX=-3e-16 StartY=1e-16 StartZ=0 EndX=-12.7 EndY=-7.33235 EndZ=0
    g11: LineSegment StartX=-3e-16 StartY=1e-16 StartZ=0 EndX=12.7 EndY=-7.33235 EndZ=0
    g12: LineSegment StartX=-3e-16 StartY=1e-16 StartZ=0 EndX=0 EndY=14.6647 EndZ=0
    g13: Circle CenterX=-3e-16 CenterY=1e-16 CenterZ=0 NormalX=0 NormalY=0 NormalZ=1 AngleXU=0 Radius=10.287
  constraints (35):
    c: PointOnObject(g2,g-2)
    c: Coincident(g3,g-1)
    c: PointOnObject(g3,g-1)
    c: PointOnObject(g3,g-1)
    c: Coincident(g4,g3)
    c: Vertical(g4)
    c: Coincident(g5,g4)
    c: Horizontal(g5)
    c: Coincident(g6,g5)
    c: Coincident(g6,g3)
    c: Vertical(g6)
    c: Equal(g2,g0)
    c: Equal(g0,g1)
    c: Coincident(g7,g2)
    c: Coincident(g7,g0)
    c: Coincident(g8,g0)
    c: Coincident(g8,g1)
    c: Coincident(g9,g1)
    c: Coincident(g9,g2)
    c: Horizontal(g8)
    c: Equal(g7,g9)
    c: Equal(g9,g8)
    c: Distance(g8) = 25.4
    c: Diameter(g2) = 3.556
    c: Coincident(g10,g3)
    c: Coincident(g10,g0)
    c: Coincident(g11,g3)
    c: Coincident(g11,g1)
    c: Coincident(g12,g3)
    c: Coincident(g12,g2)
    c: Equal(g12,g10)
    c: Radius(g3) = 25
    c: Distance(g4) = 25.4
    c: Coincident(g13,g3)
    c: Diameter(g13) = 20.574
FEATURE [PartDesign::Pad] Pad013
  Direction = (0,-1,-2e-16)
  Length = 5.08
  Length2 = 10
  Placement = pos=(0,0,0) rot=(1,0,0;1.5708rad)
  Profile = -> Sketch029
  ReferenceAxis = -> Sketch029 [N_Axis]
  Type = 0
FEATURE [Sketcher::SketchObject] Sketch030
  ExternalGeometry = -> [Pad013]
  FullyConstrained = true
  MapMode = 5
  Placement = pos=(0,0,0) rot=(-1,0,0;1.5708rad)
  Support = -> [Pad013]
  sketch-geometry (6):
    g0: ArcOfCircle CenterX=0 CenterY=0 CenterZ=0 NormalX=0 NormalY=0 NormalZ=1 AngleXU=0 Radius=20.32 StartAngle=3e-16 EndAngle=3.14159
    g1: LineSegment StartX=-20.32 StartY=-2.141e-13 StartZ=0 EndX=-25 EndY=0 EndZ=0
    g2: LineSegment StartX=-25 StartY=0 StartZ=0 EndX=-25 EndY=25.4 EndZ=0
    g3: LineSegment StartX=-25 StartY=25.4 StartZ=0 EndX=25 EndY=25.4 EndZ=0
    g4: LineSegment StartX=25 StartY=25.4 StartZ=0 EndX=25 EndY=0 EndZ=0
    g5: LineSegment StartX=25 StartY=0 StartZ=0 EndX=20.32 EndY=5.9e-15 EndZ=0
  constraints (16):
    c: Coincident(g0,g-1)
    c: PointOnObject(g0,g-1)
    c: PointOnObject(g0,g-1)
    c: Radius(g0) = 20.32
    c: Coincident(g1,g0)
    c: PointOnObject(g1,g-1)
    c: Coincident(g2,g1)
    c: Coincident(g2,g-4)
    c: Vertical(g2)
    c: Coincident(g3,g2)
    c: Coincident(g3,g-3)
    c: Coincident(g4,g3)
    c: PointOnObject(g4,g-1)
    c: Vertical(g4)
    c: Coincident(g5,g4)
    c: Coincident(g5,g0)
FEATURE [PartDesign::Pad] Pad014
  BaseFeature = -> Pad013
  Direction = (0,1,2e-16)
  Length = 40.64
  Length2 = 10
  Placement = pos=(0,0,0) rot=(1,0,0;1.5708rad)
  Profile = -> Sketch030
  ReferenceAxis = -> Sketch030 [N_Axis]
  Type = 0
FEATURE [Sketcher::SketchObject] Sketch031
  ExternalGeometry = -> [Pad014]
  FullyConstrained = true
  MapMode = 5
  Placement = pos=(0,0,1.1437e-12) rot=(0,0,1;3.14159rad)
  Support = -> [Pad014]
  sketch-geometry (8):
    g0: LineSegment StartX=-18 StartY=-1.27 StartZ=0 EndX=18 EndY=-1.27 EndZ=0
    g1: LineSegment StartX=18 StartY=-1.27 StartZ=0 EndX=18 EndY=-34.29 EndZ=0
    g2: LineSegment StartX=18 StartY=-34.29 StartZ=0 EndX=-18 EndY=-34.29 EndZ=0
    g3: LineSegment StartX=-18 StartY=-34.29 StartZ=0 EndX=-18 EndY=-1.27 EndZ=0
    g4: Circle CenterX=-18 CenterY=-1.27 CenterZ=0 NormalX=0 NormalY=0 NormalZ=1 AngleXU=0 Radius=1.27
    g5: Circle CenterX=18 CenterY=-1.27 CenterZ=0 NormalX=0 NormalY=0 NormalZ=1 AngleXU=0 Radius=1.27
    g6: Circle CenterX=18 CenterY=-34.29 CenterZ=0 NormalX=0 NormalY=0 NormalZ=1 AngleXU=0 Radius=1.27
    g7: Circle CenterX=-18 CenterY=-34.29 CenterZ=0 NormalX=0 NormalY=0 NormalZ=1 AngleXU=0 Radius=1.27
  constraints (19):
    c: Coincident(g0,g1)
    c: Coincident(g1,g2)
    c: Coincident(g2,g3)
    c: Coincident(g3,g0)
    c: Horizontal(g2)
    c: Vertical(g1)
    c: Vertical(g3)
    c: Symmetric(g0,g0,g-2)
    c: Coincident(g4,g0)
    c: Coincident(g5,g0)
    c: Coincident(g6,g1)
    c: Coincident(g7,g2)
    c: Equal(g7,g4)
    c: Equal(g4,g5)
    c: Equal(g5,g6)
    c: Diameter(g5) = 2.54
    c: Distance(g5,g-3) = 6.35
    c: Distance(g1) = 33.02
    c: Distance(g2) = 36
FEATURE [PartDesign::Hole] Hole
  BaseFeature = -> Pad014
  CustomThreadClearance = 0
  Depth = 170.573
  DepthType = 1
  Diameter = 3.5052
  DrillForDepth = false
  DrillPoint = 1
  DrillPointAngle = 118
  HoleCutCountersinkAngle = 90
  HoleCutCustomValues = false
  HoleCutDepth = 19.05
  HoleCutDiameter = 6.4008
  HoleCutType = 1
  ModelThread = false
  Placement = pos=(0,0,0) rot=(1,0,0;1.5708rad)
  Profile = -> Sketch031
  Tapered = false
  TaperedAngle = 90
  ThreadClass = 0
  ThreadDepth = 170.573
  ThreadDepthType = 0
  ThreadDirection = 0
  ThreadFit = 0
  ThreadSize = 0
  ThreadType = 0
  Threaded = false
  UseCustomThreadClearance = false
FEATURE [Sketcher::SketchObject] Sketch032
  FullyConstrained = true
  MapMode = 5
  Placement = pos=(0,0,0) rot=(1,0,0;1.5708rad)
  Support = -> [XZ_Plane015]
  sketch-geometry (4):
    g0: ArcOfCircle CenterX=0 CenterY=0 CenterZ=0 NormalX=0 NormalY=0 NormalZ=1 AngleXU=0 Radius=6.35 StartAngle=0 EndAngle=3.14159
    g1: LineSegment StartX=-6.35 StartY=8e-16 StartZ=0 EndX=-6.35 EndY=-6.35 EndZ=0
    g2: LineSegment StartX=-6.35 StartY=-6.35 StartZ=0 EndX=6.35 EndY=-6.35 EndZ=0
    g3: LineSegment StartX=6.35 StartY=-6.35 StartZ=0 EndX=6.35 EndY=0 EndZ=0
  constraints (12):
    c: Coincident(g0,g-1)
    c: PointOnObject(g0,g-1)
    c: PointOnObject(g0,g-1)
    c: Coincident(g1,g0)
    c: Vertical(g1)
    c: Coincident(g2,g1)
    c: Horizontal(g2)
    c: Coincident(g3,g2)
    c: Coincident(g3,g0)
    c: Vertical(g3)
    c: Distance(g2) = 12.7
    c: Distance(g3) = 6.35
FEATURE [PartDesign::Pad] Pad015
  Direction = (0,-1,-2e-16)
  Length = 12.7
  Length2 = 10
  Placement = pos=(0,0,0) rot=(1,0,0;1.5708rad)
  Profile = -> Sketch032
  ReferenceAxis = -> Sketch032 [N_Axis]
  Type = 0
FEATURE [PartDesign::Plane] DatumPlane002
  AttachmentOffset = pos=(0,0,-6.35) rot=(0,0,1;0rad)
  Length = 60
  MapMode = 5
  Placement = pos=(0,0,0) rot=(1,0,0;3.14159rad)
  ResizeMode = 0
  Support = -> [Pad015]
  Width = 60
FEATURE [Sketcher::SketchObject] Sketch033
  ExternalGeometry = -> [Pad015]
  FullyConstrained = true
  MapMode = 5
  Placement = pos=(0,0,0) rot=(1,0,0;3.14159rad)
  Support = -> [DatumPlane002]
  sketch-geometry (2):
    g0: Circle CenterX=0 CenterY=6.35 CenterZ=0 NormalX=0 NormalY=0 NormalZ=1 AngleXU=0 Radius=3.8862
    g1: GeomPoint X=0 Y=12.7 Z=0
  constraints (4):
    c: PointOnObject(g1,g-3)
    c: PointOnObject(g1,g-2)
    c: Symmetric(g1,g-1,g0)
    c: Diameter(g0) = 7.7724
FEATURE [PartDesign::Pad] Pad016
  BaseFeature = -> Pad015
  Direction = (0,-2e-16,-1)
  Length = 25.4
  Length2 = 10
  Placement = pos=(0,0,0) rot=(1,0,0;1.5708rad)
  Profile = -> Sketch033
  ReferenceAxis = -> Sketch033 [N_Axis]
  Reversed = true
  Type = 0
FEATURE [Sketcher::SketchObject] Sketch034
  FullyConstrained = true
  MapMode = 5
  Placement = pos=(0,-12.7,1.4e-15) rot=(1,0,0;1.5708rad)
  Support = -> [Pad016]
  sketch-geometry (3):
    g0: ArcOfCircle CenterX=0 CenterY=0 CenterZ=0 NormalX=0 NormalY=0 NormalZ=1 AngleXU=0 Radius=3.0988 StartAngle=2.13269 EndAngle=7.29209
    g1: LineSegment StartX=-1.651 StartY=2.62236 StartZ=0 EndX=1.651 EndY=2.62236 EndZ=0
    g2: LineSegment StartX=0 StartY=2.62236 StartZ=0 EndX=0 EndY=-3.0988 EndZ=0
  constraints (10):
    c: Coincident(g0,g-1)
    c: Coincident(g1,g0)
    c: Coincident(g1,g0)
    c: Horizontal(g1)
    c: Radius(g0) = 3.0988
    c: PointOnObject(g2,g1)
    c: PointOnObject(g2,g0)
    c: Vertical(g2)
    c: PointOnObject(g0,g2)
    c: Distance(g1) = 3.302
FEATURE [PartDesign::Pocket] Pocket016
  BaseFeature = -> Pad016
  Direction = (0,1,-2e-16)
  Length = 5
  Length2 = 5
  Placement = pos=(0,0,0) rot=(1,0,0;1.5708rad)
  Profile = -> Sketch034
  ReferenceAxis = -> Sketch034 [N_Axis]
  Type = 1
FEATURE [PartDesign::Body] Body014  label="Swingarm"
  Group = -> [Sketch032,Pad015,DatumPlane002,Sketch033,Pad016,Sketch034,Pocket016]
  Origin = -> Origin015
  Tip = -> Pocket016
FEATURE [Sketcher::SketchObject] Sketch035
  ExternalGeometry = -> [Hole]
  FullyConstrained = true
  MapMode = 5
  Placement = pos=(0,40.64,9e-15) rot=(-1,0,0;1.5708rad)
  Support = -> [Hole]
  sketch-geometry (5):
    g0: LineSegment StartX=0 StartY=0 StartZ=0 EndX=25 EndY=14.4338 EndZ=0
    g1: LineSegment StartX=25 StartY=14.4338 StartZ=0 EndX=25 EndY=0 EndZ=0
    g2: LineSegment StartX=25 StartY=0 StartZ=0 EndX=-25 EndY=0 EndZ=0
    g3: LineSegment StartX=-25 StartY=0 StartZ=0 EndX=-25 EndY=14.4338 EndZ=0
    g4: LineSegment StartX=-25 StartY=14.4338 StartZ=0 EndX=0 EndY=0 EndZ=0
  constraints (14):
    c: Coincident(g0,g-1)
    c: Coincident(g1,g0)
    c: PointOnObject(g1,g-1)
    c: Vertical(g1)
    c: Coincident(g2,g1)
    c: Horizontal(g2)
    c: Coincident(g3,g2)
    c: Coincident(g4,g3)
    c: Coincident(g4,g0)
    c: Vertical(g3)
    c: Equal(g4,g0)
    c: Equal(g3,g1)
    c: PointOnObject(g3,g-3)
    c: Angle(g2,g4) = 2.61799
FEATURE [PartDesign::Pocket] Pocket017
  BaseFeature = -> Hole
  Direction = (0,-1,-2e-16)
  Length = 15.24
  Length2 = 5
  Placement = pos=(0,0,0) rot=(1,0,0;1.5708rad)
  Profile = -> Sketch035
  ReferenceAxis = -> Sketch035 [N_Axis]
  Type = 0
FEATURE [Sketcher::SketchObject] Sketch036
  ExternalGeometry = -> [Pocket017]
  FullyConstrained = true
  MapMode = 5
  Placement = pos=(0,-5.08,-1.1e-15) rot=(1,0,0;1.5708rad)
  Support = -> [Pocket017]
  sketch-geometry (3):
    g0: Circle CenterX=12.7 CenterY=-7.33235 CenterZ=0 NormalX=0 NormalY=0 NormalZ=1 AngleXU=0 Radius=2.921
    g1: Circle CenterX=0 CenterY=14.6647 CenterZ=0 NormalX=0 NormalY=0 NormalZ=1 AngleXU=0 Radius=2.921
    g2: Circle CenterX=-12.7 CenterY=-7.33235 CenterZ=0 NormalX=0 NormalY=0 NormalZ=1 AngleXU=0 Radius=2.921
  constraints (6):
    c: Coincident(g0,g-3)
    c: Coincident(g1,g-4)
    c: Coincident(g2,g-5)
    c: Equal(g2,g0)
    c: Equal(g0,g1)
    c: Diameter(g1) = 5.842
FEATURE [PartDesign::Pocket] Pocket018
  BaseFeature = -> Pocket017
  Direction = (0,1,2e-16)
  Length = 1.778
  Length2 = 5
  Placement = pos=(0,0,0) rot=(1,0,0;1.5708rad)
  Profile = -> Sketch036
  ReferenceAxis = -> Sketch036 [N_Axis]
  Type = 0
FEATURE [PartDesign::Fillet] Fillet
  Base = -> Pocket018 [Edge61,Edge59,Edge54,Edge57]
  BaseFeature = -> Pocket018
  Placement = pos=(0,0,0) rot=(1,0,0;1.5708rad)
  Radius = 1.524
  SupportTransform = false
  UseAllEdges = false
FEATURE [PartDesign::Fillet] Fillet001
  Base = -> Fillet [Edge66,Edge28]
  BaseFeature = -> Fillet
  Placement = pos=(0,0,0) rot=(1,0,0;1.5708rad)
  Radius = 5.08
  SupportTransform = false
  UseAllEdges = false
FEATURE [PartDesign::Chamfer] Chamfer
  Angle = 45
  Base = -> Fillet001 [Edge119,Edge118,Edge117]
  BaseFeature = -> Fillet001
  ChamferType = 0
  FlipDirection = false
  Placement = pos=(0,0,0) rot=(1,0,0;1.5708rad)
  Size = 0.508
  Size2 = 1
  SupportTransform = false
  UseAllEdges = false
FEATURE [PartDesign::Body] Body013  label="EncoderHolder"
  Group = -> [Sketch029,Pad013,Sketch030,Pad014,Sketch031,Hole,Sketch035,Pocket017,Sketch036,Pocket018,Fillet,Fillet001,Chamfer]
  Origin = -> Origin014
  Tip = -> Chamfer
FEATURE [App::DocumentObjectGroup] Parts
  Group = -> [Body,Body001,Body002,Body003,Body004,Body005,Body006,Body007,Part__Feature,Body008,Body009,Body010,Body011,Body012,Body013,Body014]
FEATURE [TechDraw::DrawViewPart] View
  CoarseView = false
  Direction = (0.57735,-0.57735,0.57735)
  Focus = 100
  HardHidden = false
  IsoCount = 0
  IsoHidden = false
  IsoVisible = false
  LockPosition = false
  Perspective = false
  Rotation = 0
  Scale = 0.14
  ScaleType = 2
  SeamHidden = false
  SeamVisible = true
  SmoothHidden = false
  SmoothVisible = true
  Source = -> [Body,Body001,Body002,Body003,Parts,Model,Body004,Body005,Body006,Body007,Part__Feature,Template,ProjGroup,ProjItem,ProjItem001,Detail,Dimension002,Dimension003,Dimension004,Annotation,Dimension,Dimension005,Dimension006,Body008,Body009,Template001,Body010,Body011]
  X = 223.045
  XDirection = (0.707107,0.707107,-7.127e-09)
  Y = 147.896
FEATURE [TechDraw::DrawPage] Page001  label="Body Assembly"
  KeepUpdated = true
  NextBalloonIndex = 1
  ProjectionType = 0
  Template = -> Template001
  Views = -> [View,View001,View002,Dimension007,Dimension008,Dimension009,Dimension010,Dimension011,Dimension012,Dimension013,Dimension014,Dimension015,Dimension016]
note: 1 file-system path scrubbed to <path> (originals preserved in the JSON sidecar)
